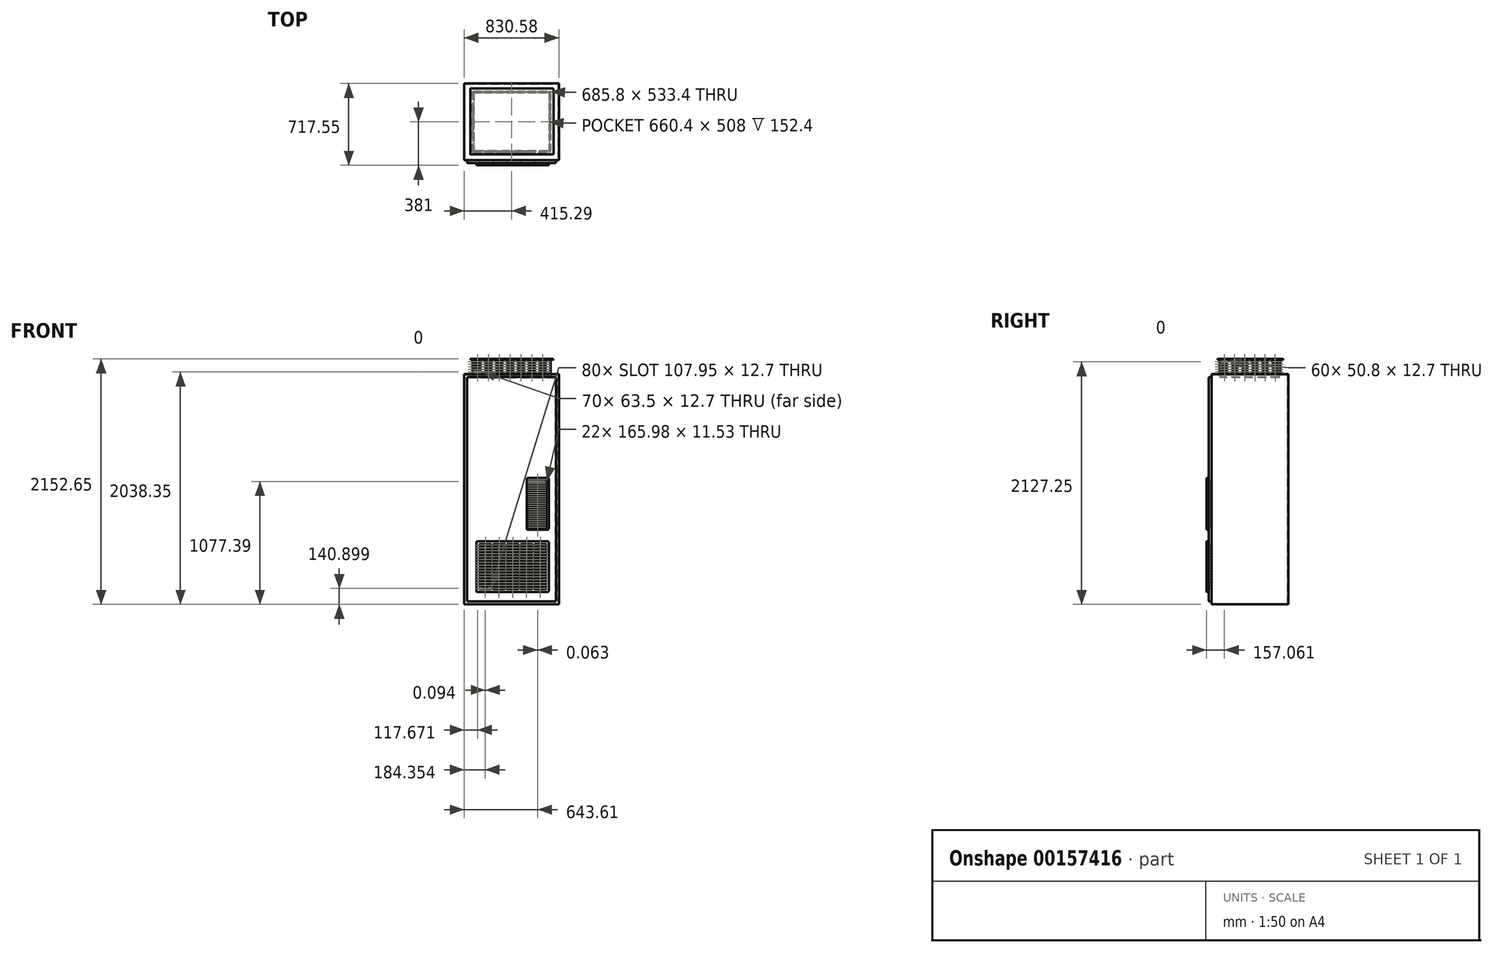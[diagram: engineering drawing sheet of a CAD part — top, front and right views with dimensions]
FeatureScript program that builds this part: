
annotation { "Feature Type Name" : "Feature", "Feature Type Description" : "" }
export const myFeature = defineFeature(function(context is Context, id is Id, definition is map)
    precondition{}
    {
        {
            var Q0;
            Q0=qCreatedBy(makeId("Front.planeOp"),FACE);
            var sketch = newSketch(context, id + "F0", { "sketchPlane" : qUnion([Q0])});
            skLineSegment(sketch, "E0.bottom", {"start": v(0, 0) * mm, "end": v(830.58, 0) * mm});
            skLineSegment(sketch, "E0.top", {"start": v(0, 2019.3) * mm, "end": v(830.58, 2019.3) * mm});
            skLineSegment(sketch, "E0.left", {"start": v(0, 0) * mm, "end": v(0, 2019.3) * mm});
            skLineSegment(sketch, "E0.right", {"start": v(830.58, 0) * mm, "end": v(830.58, 2019.3) * mm});
            skSolve(sketch);
        }
        {
            var Q0;
            Q0 = qSketchRegion(id + "F0", true);
            extrude(context, id + "F1", {"entities" : qUnion([Q0]), "depth" : 673.1 * mm});
        }
        {
            var Q0;
            Q0=makeQuery(id+"F1.opExtrude","CAP_FACE",FACE,{"disambiguationData":[OSD([sQuery(id+"F0.wireOp",EDGE,"E0.bottom"),sQuery(id+"F0.wireOp",EDGE,"E0.top"),sQuery(id+"F0.wireOp",EDGE,"E0.left"),sQuery(id+"F0.wireOp",EDGE,"E0.right")])],"isStart":false});
            var sketch = newSketch(context, id + "F2", { "sketchPlane" : qUnion([Q0])});
            skLineSegment(sketch, "E1.bottom", {"start": v(25.4, 25.4) * mm, "end": v(805.18, 25.4) * mm});
            skLineSegment(sketch, "E1.top", {"start": v(25.4, 1993.9) * mm, "end": v(805.18, 1993.9) * mm});
            skLineSegment(sketch, "E1.left", {"start": v(25.4, 25.4) * mm, "end": v(25.4, 1993.9) * mm});
            skLineSegment(sketch, "E1.right", {"start": v(805.18, 25.4) * mm, "end": v(805.18, 1993.9) * mm});
            skSolve(sketch);
        }
        {
            var Q0;
            Q0 = qSketchRegion(id + "F2", true);
            extrude(context, id + "F3", {"entities" : qUnion([Q0]), "operationType" : NewBodyOperationType.ADD, "depth" : 25.4 * mm});
        }
        {
            var Q0;
            Q0=makeQuery(id+"F3.opExtrude","CAP_EDGE",EDGE,{"disambiguationData":[OSD([sQuery(id+"F2.wireOp",EDGE,"E1.bottom")])],"isStart":false});
            var Q1;
            Q1=makeQuery(id+"F3.opExtrude","CAP_EDGE",EDGE,{"disambiguationData":[OSD([sQuery(id+"F2.wireOp",EDGE,"E1.left")])],"isStart":false});
            var Q2;
            Q2=makeQuery(id+"F3.opExtrude","CAP_EDGE",EDGE,{"disambiguationData":[OSD([sQuery(id+"F2.wireOp",EDGE,"E1.right")])],"isStart":false});
            var Q3;
            Q3=makeQuery(id+"F3.opExtrude","CAP_EDGE",EDGE,{"disambiguationData":[OSD([sQuery(id+"F2.wireOp",EDGE,"E1.top")])],"isStart":false});
            var Q4;
            Q4=makeQuery(id+"F3.opExtrude","SWEPT_EDGE",EDGE,{"disambiguationData":[OSD([sQuery(id+"F2.wireOp",EDGE,"E1.top"),sQuery(id+"F2.wireOp",EDGE,"E1.left")])]});
            var Q5;
            Q5=makeQuery(id+"F3.opExtrude","SWEPT_EDGE",EDGE,{"disambiguationData":[OSD([sQuery(id+"F2.wireOp",EDGE,"E1.top"),sQuery(id+"F2.wireOp",EDGE,"E1.right")])]});
            var Q6;
            Q6=makeQuery(id+"F3.opExtrude","SWEPT_EDGE",EDGE,{"disambiguationData":[OSD([sQuery(id+"F2.wireOp",EDGE,"E1.bottom"),sQuery(id+"F2.wireOp",EDGE,"E1.right")])]});
            var Q7;
            Q7=makeQuery(id+"F3.opExtrude","SWEPT_EDGE",EDGE,{"disambiguationData":[OSD([sQuery(id+"F2.wireOp",EDGE,"E1.bottom"),sQuery(id+"F2.wireOp",EDGE,"E1.left")])]});
            fillet(context, id + "F4", {"entities" : qUnion([Q0, Q1, Q2, Q3, Q4, Q5, Q6, Q7]), "radius" : 9.52 * mm, "tangentPropagation" : true, "allowEdgeOverflow" : false});
        }
        {
            var Q0;
            Q0=makeQuery(id+"F1.opExtrude","SWEPT_FACE",FACE,{"disambiguationData":[OSD([sQuery(id+"F0.wireOp",EDGE,"E0.top")])]});
            var sketch = newSketch(context, id + "F5", { "sketchPlane" : qUnion([Q0])});
            skLineSegment(sketch, "E2.bottom", {"start": v(72.39, -603.25) * mm, "end": v(758.19, -603.25) * mm});
            skLineSegment(sketch, "E2.top", {"start": v(72.39, -69.85) * mm, "end": v(758.19, -69.85) * mm});
            skLineSegment(sketch, "E2.left", {"start": v(72.39, -603.25) * mm, "end": v(72.39, -69.85) * mm});
            skLineSegment(sketch, "E2.right", {"start": v(758.19, -603.25) * mm, "end": v(758.19, -69.85) * mm});
            skSolve(sketch);
        }
        {
            var Q0;
            Q0 = qSketchRegion(id + "F5", true);
            extrude(context, id + "F6", {"entities" : qUnion([Q0]), "operationType" : NewBodyOperationType.ADD, "depth" : 127 * mm});
        }
        {
            var Q0;
            Q0=makeQuery(id+"F6.opExtrude","SWEPT_FACE",FACE,{"disambiguationData":[OSD([sQuery(id+"F5.wireOp",EDGE,"E2.bottom")])]});
            var sketch = newSketch(context, id + "F7", { "sketchPlane" : qUnion([Q0])});
            skLineSegment(sketch, "E3.bottom", {"start": v(85.92, 2133.6) * mm, "end": v(149.42, 2133.6) * mm});
            skLineSegment(sketch, "E3.top", {"start": v(85.92, 2120.9) * mm, "end": v(149.42, 2120.9) * mm});
            skLineSegment(sketch, "E3.left", {"start": v(85.92, 2133.6) * mm, "end": v(85.92, 2120.9) * mm});
            skLineSegment(sketch, "E3.right", {"start": v(149.42, 2133.6) * mm, "end": v(149.42, 2120.9) * mm});
            skLineSegment(sketch, "E4.bottom", {"start": v(85.92, 2111.38) * mm, "end": v(149.42, 2111.38) * mm});
            skLineSegment(sketch, "E4.top", {"start": v(85.92, 2098.67) * mm, "end": v(149.42, 2098.67) * mm});
            skLineSegment(sketch, "E4.left", {"start": v(85.92, 2111.38) * mm, "end": v(85.92, 2098.67) * mm});
            skLineSegment(sketch, "E4.right", {"start": v(149.42, 2111.38) * mm, "end": v(149.42, 2098.67) * mm});
            skLineSegment(sketch, "E5.bottom", {"start": v(85.92, 2089.15) * mm, "end": v(149.42, 2089.15) * mm});
            skLineSegment(sketch, "E5.top", {"start": v(85.92, 2076.45) * mm, "end": v(149.42, 2076.45) * mm});
            skLineSegment(sketch, "E5.left", {"start": v(85.92, 2089.15) * mm, "end": v(85.92, 2076.45) * mm});
            skLineSegment(sketch, "E5.right", {"start": v(149.42, 2089.15) * mm, "end": v(149.42, 2076.45) * mm});
            skLineSegment(sketch, "E6.bottom", {"start": v(85.92, 2066.92) * mm, "end": v(149.42, 2066.92) * mm});
            skLineSegment(sketch, "E6.top", {"start": v(85.92, 2054.22) * mm, "end": v(149.42, 2054.22) * mm});
            skLineSegment(sketch, "E6.left", {"start": v(85.92, 2066.92) * mm, "end": v(85.92, 2054.22) * mm});
            skLineSegment(sketch, "E6.right", {"start": v(149.42, 2066.92) * mm, "end": v(149.42, 2054.22) * mm});
            skLineSegment(sketch, "E7.bottom", {"start": v(85.92, 2044.7) * mm, "end": v(149.42, 2044.7) * mm});
            skLineSegment(sketch, "E7.top", {"start": v(85.92, 2032) * mm, "end": v(149.42, 2032) * mm});
            skLineSegment(sketch, "E7.left", {"start": v(85.92, 2044.7) * mm, "end": v(85.92, 2032) * mm});
            skLineSegment(sketch, "E7.right", {"start": v(149.42, 2044.7) * mm, "end": v(149.42, 2032) * mm});
            skLineSegment(sketch, "E8.1.0.0", {"start": v(181.17, 2044.7) * mm, "end": v(244.67, 2044.7) * mm});
            skLineSegment(sketch, "E8.1.0.1", {"start": v(181.17, 2066.92) * mm, "end": v(244.67, 2066.92) * mm});
            skLineSegment(sketch, "E8.1.0.2", {"start": v(181.17, 2120.9) * mm, "end": v(244.67, 2120.9) * mm});
            skLineSegment(sketch, "E8.1.0.3", {"start": v(181.17, 2133.6) * mm, "end": v(244.67, 2133.6) * mm});
            skLineSegment(sketch, "E8.1.0.4", {"start": v(181.17, 2054.22) * mm, "end": v(244.67, 2054.22) * mm});
            skLineSegment(sketch, "E8.1.0.5", {"start": v(181.17, 2111.38) * mm, "end": v(181.17, 2098.67) * mm});
            skLineSegment(sketch, "E8.1.0.6", {"start": v(181.17, 2133.6) * mm, "end": v(181.17, 2120.9) * mm});
            skLineSegment(sketch, "E8.1.0.7", {"start": v(181.17, 2044.7) * mm, "end": v(181.17, 2032) * mm});
            skLineSegment(sketch, "E8.1.0.8", {"start": v(181.17, 2089.15) * mm, "end": v(244.67, 2089.15) * mm});
            skLineSegment(sketch, "E8.1.0.9", {"start": v(244.67, 2133.6) * mm, "end": v(244.67, 2120.9) * mm});
            skLineSegment(sketch, "E8.1.0.10", {"start": v(181.17, 2111.38) * mm, "end": v(244.67, 2111.38) * mm});
            skLineSegment(sketch, "E8.1.0.11", {"start": v(244.67, 2111.38) * mm, "end": v(244.67, 2098.67) * mm});
            skLineSegment(sketch, "E8.1.0.12", {"start": v(244.67, 2044.7) * mm, "end": v(244.67, 2032) * mm});
            skLineSegment(sketch, "E8.1.0.13", {"start": v(181.17, 2032) * mm, "end": v(244.67, 2032) * mm});
            skLineSegment(sketch, "E8.1.0.14", {"start": v(181.17, 2066.92) * mm, "end": v(181.17, 2054.22) * mm});
            skLineSegment(sketch, "E8.1.0.15", {"start": v(244.67, 2066.92) * mm, "end": v(244.67, 2054.22) * mm});
            skLineSegment(sketch, "E8.1.0.16", {"start": v(244.67, 2089.15) * mm, "end": v(244.67, 2076.45) * mm});
            skLineSegment(sketch, "E8.1.0.17", {"start": v(181.17, 2098.67) * mm, "end": v(244.67, 2098.67) * mm});
            skLineSegment(sketch, "E8.1.0.18", {"start": v(181.17, 2076.45) * mm, "end": v(244.67, 2076.45) * mm});
            skLineSegment(sketch, "E8.1.0.19", {"start": v(181.17, 2089.15) * mm, "end": v(181.17, 2076.45) * mm});
            skLineSegment(sketch, "E8.2.0.0", {"start": v(276.42, 2044.7) * mm, "end": v(339.92, 2044.7) * mm});
            skLineSegment(sketch, "E8.2.0.1", {"start": v(276.42, 2066.92) * mm, "end": v(339.92, 2066.92) * mm});
            skLineSegment(sketch, "E8.2.0.2", {"start": v(276.42, 2120.9) * mm, "end": v(339.92, 2120.9) * mm});
            skLineSegment(sketch, "E8.2.0.3", {"start": v(276.42, 2133.6) * mm, "end": v(339.92, 2133.6) * mm});
            skLineSegment(sketch, "E8.2.0.4", {"start": v(276.42, 2054.22) * mm, "end": v(339.92, 2054.22) * mm});
            skLineSegment(sketch, "E8.2.0.5", {"start": v(276.42, 2111.38) * mm, "end": v(276.42, 2098.67) * mm});
            skLineSegment(sketch, "E8.2.0.6", {"start": v(276.42, 2133.6) * mm, "end": v(276.42, 2120.9) * mm});
            skLineSegment(sketch, "E8.2.0.7", {"start": v(276.42, 2044.7) * mm, "end": v(276.42, 2032) * mm});
            skLineSegment(sketch, "E8.2.0.8", {"start": v(276.42, 2089.15) * mm, "end": v(339.92, 2089.15) * mm});
            skLineSegment(sketch, "E8.2.0.9", {"start": v(339.92, 2133.6) * mm, "end": v(339.92, 2120.9) * mm});
            skLineSegment(sketch, "E8.2.0.10", {"start": v(276.42, 2111.38) * mm, "end": v(339.92, 2111.38) * mm});
            skLineSegment(sketch, "E8.2.0.11", {"start": v(339.92, 2111.38) * mm, "end": v(339.92, 2098.67) * mm});
            skLineSegment(sketch, "E8.2.0.12", {"start": v(339.92, 2044.7) * mm, "end": v(339.92, 2032) * mm});
            skLineSegment(sketch, "E8.2.0.13", {"start": v(276.42, 2032) * mm, "end": v(339.92, 2032) * mm});
            skLineSegment(sketch, "E8.2.0.14", {"start": v(276.42, 2066.92) * mm, "end": v(276.42, 2054.22) * mm});
            skLineSegment(sketch, "E8.2.0.15", {"start": v(339.92, 2066.92) * mm, "end": v(339.92, 2054.22) * mm});
            skLineSegment(sketch, "E8.2.0.16", {"start": v(339.92, 2089.15) * mm, "end": v(339.92, 2076.45) * mm});
            skLineSegment(sketch, "E8.2.0.17", {"start": v(276.42, 2098.67) * mm, "end": v(339.92, 2098.67) * mm});
            skLineSegment(sketch, "E8.2.0.18", {"start": v(276.42, 2076.45) * mm, "end": v(339.92, 2076.45) * mm});
            skLineSegment(sketch, "E8.2.0.19", {"start": v(276.42, 2089.15) * mm, "end": v(276.42, 2076.45) * mm});
            skLineSegment(sketch, "E8.3.0.0", {"start": v(371.67, 2044.7) * mm, "end": v(435.17, 2044.7) * mm});
            skLineSegment(sketch, "E8.3.0.1", {"start": v(371.67, 2066.92) * mm, "end": v(435.17, 2066.92) * mm});
            skLineSegment(sketch, "E8.3.0.2", {"start": v(371.67, 2120.9) * mm, "end": v(435.17, 2120.9) * mm});
            skLineSegment(sketch, "E8.3.0.3", {"start": v(371.67, 2133.6) * mm, "end": v(435.17, 2133.6) * mm});
            skLineSegment(sketch, "E8.3.0.4", {"start": v(371.67, 2054.22) * mm, "end": v(435.17, 2054.22) * mm});
            skLineSegment(sketch, "E8.3.0.5", {"start": v(371.67, 2111.38) * mm, "end": v(371.67, 2098.67) * mm});
            skLineSegment(sketch, "E8.3.0.6", {"start": v(371.67, 2133.6) * mm, "end": v(371.67, 2120.9) * mm});
            skLineSegment(sketch, "E8.3.0.7", {"start": v(371.67, 2044.7) * mm, "end": v(371.67, 2032) * mm});
            skLineSegment(sketch, "E8.3.0.8", {"start": v(371.67, 2089.15) * mm, "end": v(435.17, 2089.15) * mm});
            skLineSegment(sketch, "E8.3.0.9", {"start": v(435.17, 2133.6) * mm, "end": v(435.17, 2120.9) * mm});
            skLineSegment(sketch, "E8.3.0.10", {"start": v(371.67, 2111.38) * mm, "end": v(435.17, 2111.38) * mm});
            skLineSegment(sketch, "E8.3.0.11", {"start": v(435.17, 2111.38) * mm, "end": v(435.17, 2098.67) * mm});
            skLineSegment(sketch, "E8.3.0.12", {"start": v(435.17, 2044.7) * mm, "end": v(435.17, 2032) * mm});
            skLineSegment(sketch, "E8.3.0.13", {"start": v(371.67, 2032) * mm, "end": v(435.17, 2032) * mm});
            skLineSegment(sketch, "E8.3.0.14", {"start": v(371.67, 2066.92) * mm, "end": v(371.67, 2054.22) * mm});
            skLineSegment(sketch, "E8.3.0.15", {"start": v(435.17, 2066.92) * mm, "end": v(435.17, 2054.22) * mm});
            skLineSegment(sketch, "E8.3.0.16", {"start": v(435.17, 2089.15) * mm, "end": v(435.17, 2076.45) * mm});
            skLineSegment(sketch, "E8.3.0.17", {"start": v(371.67, 2098.67) * mm, "end": v(435.17, 2098.67) * mm});
            skLineSegment(sketch, "E8.3.0.18", {"start": v(371.67, 2076.45) * mm, "end": v(435.17, 2076.45) * mm});
            skLineSegment(sketch, "E8.3.0.19", {"start": v(371.67, 2089.15) * mm, "end": v(371.67, 2076.45) * mm});
            skLineSegment(sketch, "E8.4.0.0", {"start": v(466.92, 2044.7) * mm, "end": v(530.42, 2044.7) * mm});
            skLineSegment(sketch, "E8.4.0.1", {"start": v(466.92, 2066.92) * mm, "end": v(530.42, 2066.92) * mm});
            skLineSegment(sketch, "E8.4.0.2", {"start": v(466.92, 2120.9) * mm, "end": v(530.42, 2120.9) * mm});
            skLineSegment(sketch, "E8.4.0.3", {"start": v(466.92, 2133.6) * mm, "end": v(530.42, 2133.6) * mm});
            skLineSegment(sketch, "E8.4.0.4", {"start": v(466.92, 2054.22) * mm, "end": v(530.42, 2054.22) * mm});
            skLineSegment(sketch, "E8.4.0.5", {"start": v(466.92, 2111.38) * mm, "end": v(466.92, 2098.67) * mm});
            skLineSegment(sketch, "E8.4.0.6", {"start": v(466.92, 2133.6) * mm, "end": v(466.92, 2120.9) * mm});
            skLineSegment(sketch, "E8.4.0.7", {"start": v(466.92, 2044.7) * mm, "end": v(466.92, 2032) * mm});
            skLineSegment(sketch, "E8.4.0.8", {"start": v(466.92, 2089.15) * mm, "end": v(530.42, 2089.15) * mm});
            skLineSegment(sketch, "E8.4.0.9", {"start": v(530.42, 2133.6) * mm, "end": v(530.42, 2120.9) * mm});
            skLineSegment(sketch, "E8.4.0.10", {"start": v(466.92, 2111.38) * mm, "end": v(530.42, 2111.38) * mm});
            skLineSegment(sketch, "E8.4.0.11", {"start": v(530.42, 2111.38) * mm, "end": v(530.42, 2098.67) * mm});
            skLineSegment(sketch, "E8.4.0.12", {"start": v(530.42, 2044.7) * mm, "end": v(530.42, 2032) * mm});
            skLineSegment(sketch, "E8.4.0.13", {"start": v(466.92, 2032) * mm, "end": v(530.42, 2032) * mm});
            skLineSegment(sketch, "E8.4.0.14", {"start": v(466.92, 2066.92) * mm, "end": v(466.92, 2054.22) * mm});
            skLineSegment(sketch, "E8.4.0.15", {"start": v(530.42, 2066.92) * mm, "end": v(530.42, 2054.22) * mm});
            skLineSegment(sketch, "E8.4.0.16", {"start": v(530.42, 2089.15) * mm, "end": v(530.42, 2076.45) * mm});
            skLineSegment(sketch, "E8.4.0.17", {"start": v(466.92, 2098.67) * mm, "end": v(530.42, 2098.67) * mm});
            skLineSegment(sketch, "E8.4.0.18", {"start": v(466.92, 2076.45) * mm, "end": v(530.42, 2076.45) * mm});
            skLineSegment(sketch, "E8.4.0.19", {"start": v(466.92, 2089.15) * mm, "end": v(466.92, 2076.45) * mm});
            skLineSegment(sketch, "E8.5.0.0", {"start": v(562.17, 2044.7) * mm, "end": v(625.67, 2044.7) * mm});
            skLineSegment(sketch, "E8.5.0.1", {"start": v(562.17, 2066.92) * mm, "end": v(625.67, 2066.92) * mm});
            skLineSegment(sketch, "E8.5.0.2", {"start": v(562.17, 2120.9) * mm, "end": v(625.67, 2120.9) * mm});
            skLineSegment(sketch, "E8.5.0.3", {"start": v(562.17, 2133.6) * mm, "end": v(625.67, 2133.6) * mm});
            skLineSegment(sketch, "E8.5.0.4", {"start": v(562.17, 2054.22) * mm, "end": v(625.67, 2054.22) * mm});
            skLineSegment(sketch, "E8.5.0.5", {"start": v(562.17, 2111.38) * mm, "end": v(562.17, 2098.67) * mm});
            skLineSegment(sketch, "E8.5.0.6", {"start": v(562.17, 2133.6) * mm, "end": v(562.17, 2120.9) * mm});
            skLineSegment(sketch, "E8.5.0.7", {"start": v(562.17, 2044.7) * mm, "end": v(562.17, 2032) * mm});
            skLineSegment(sketch, "E8.5.0.8", {"start": v(562.17, 2089.15) * mm, "end": v(625.67, 2089.15) * mm});
            skLineSegment(sketch, "E8.5.0.9", {"start": v(625.67, 2133.6) * mm, "end": v(625.67, 2120.9) * mm});
            skLineSegment(sketch, "E8.5.0.10", {"start": v(562.17, 2111.38) * mm, "end": v(625.67, 2111.38) * mm});
            skLineSegment(sketch, "E8.5.0.11", {"start": v(625.67, 2111.38) * mm, "end": v(625.67, 2098.67) * mm});
            skLineSegment(sketch, "E8.5.0.12", {"start": v(625.67, 2044.7) * mm, "end": v(625.67, 2032) * mm});
            skLineSegment(sketch, "E8.5.0.13", {"start": v(562.17, 2032) * mm, "end": v(625.67, 2032) * mm});
            skLineSegment(sketch, "E8.5.0.14", {"start": v(562.17, 2066.92) * mm, "end": v(562.17, 2054.22) * mm});
            skLineSegment(sketch, "E8.5.0.15", {"start": v(625.67, 2066.92) * mm, "end": v(625.67, 2054.22) * mm});
            skLineSegment(sketch, "E8.5.0.16", {"start": v(625.67, 2089.15) * mm, "end": v(625.67, 2076.45) * mm});
            skLineSegment(sketch, "E8.5.0.17", {"start": v(562.17, 2098.67) * mm, "end": v(625.67, 2098.67) * mm});
            skLineSegment(sketch, "E8.5.0.18", {"start": v(562.17, 2076.45) * mm, "end": v(625.67, 2076.45) * mm});
            skLineSegment(sketch, "E8.5.0.19", {"start": v(562.17, 2089.15) * mm, "end": v(562.17, 2076.45) * mm});
            skLineSegment(sketch, "E8.6.0.0", {"start": v(657.42, 2044.7) * mm, "end": v(720.92, 2044.7) * mm});
            skLineSegment(sketch, "E8.6.0.1", {"start": v(657.42, 2066.92) * mm, "end": v(720.92, 2066.92) * mm});
            skLineSegment(sketch, "E8.6.0.2", {"start": v(657.42, 2120.9) * mm, "end": v(720.92, 2120.9) * mm});
            skLineSegment(sketch, "E8.6.0.3", {"start": v(657.42, 2133.6) * mm, "end": v(720.92, 2133.6) * mm});
            skLineSegment(sketch, "E8.6.0.4", {"start": v(657.42, 2054.22) * mm, "end": v(720.92, 2054.22) * mm});
            skLineSegment(sketch, "E8.6.0.5", {"start": v(657.42, 2111.38) * mm, "end": v(657.42, 2098.67) * mm});
            skLineSegment(sketch, "E8.6.0.6", {"start": v(657.42, 2133.6) * mm, "end": v(657.42, 2120.9) * mm});
            skLineSegment(sketch, "E8.6.0.7", {"start": v(657.42, 2044.7) * mm, "end": v(657.42, 2032) * mm});
            skLineSegment(sketch, "E8.6.0.8", {"start": v(657.42, 2089.15) * mm, "end": v(720.92, 2089.15) * mm});
            skLineSegment(sketch, "E8.6.0.9", {"start": v(720.92, 2133.6) * mm, "end": v(720.92, 2120.9) * mm});
            skLineSegment(sketch, "E8.6.0.10", {"start": v(657.42, 2111.38) * mm, "end": v(720.92, 2111.38) * mm});
            skLineSegment(sketch, "E8.6.0.11", {"start": v(720.92, 2111.38) * mm, "end": v(720.92, 2098.67) * mm});
            skLineSegment(sketch, "E8.6.0.12", {"start": v(720.92, 2044.7) * mm, "end": v(720.92, 2032) * mm});
            skLineSegment(sketch, "E8.6.0.13", {"start": v(657.42, 2032) * mm, "end": v(720.92, 2032) * mm});
            skLineSegment(sketch, "E8.6.0.14", {"start": v(657.42, 2066.92) * mm, "end": v(657.42, 2054.22) * mm});
            skLineSegment(sketch, "E8.6.0.15", {"start": v(720.92, 2066.92) * mm, "end": v(720.92, 2054.22) * mm});
            skLineSegment(sketch, "E8.6.0.16", {"start": v(720.92, 2089.15) * mm, "end": v(720.92, 2076.45) * mm});
            skLineSegment(sketch, "E8.6.0.17", {"start": v(657.42, 2098.67) * mm, "end": v(720.92, 2098.67) * mm});
            skLineSegment(sketch, "E8.6.0.18", {"start": v(657.42, 2076.45) * mm, "end": v(720.92, 2076.45) * mm});
            skLineSegment(sketch, "E8.6.0.19", {"start": v(657.42, 2089.15) * mm, "end": v(657.42, 2076.45) * mm});
            skSolve(sketch);
        }
        {
            var Q0;
            Q0 = qSketchRegion(id + "F7", true);
            extrude(context, id + "F8", {"entities" : qUnion([Q0]), "operationType" : NewBodyOperationType.REMOVE, "endBound" : BoundingType.THROUGH_ALL, "oppositeDirection" : true, "depth" : 25.4 * mm});
        }
        {
            var Q0;
            Q0=makeQuery(id+"F6.opExtrude","SWEPT_FACE",FACE,{"disambiguationData":[OSD([sQuery(id+"F5.wireOp",EDGE,"E2.left")])]});
            var sketch = newSketch(context, id + "F9", { "sketchPlane" : qUnion([Q0])});
            skLineSegment(sketch, "E9.bottom", {"start": v(90.59, 2133.6) * mm, "end": v(141.39, 2133.6) * mm});
            skLineSegment(sketch, "E9.top", {"start": v(90.59, 2120.9) * mm, "end": v(141.39, 2120.9) * mm});
            skLineSegment(sketch, "E9.left", {"start": v(90.59, 2133.6) * mm, "end": v(90.59, 2120.9) * mm});
            skLineSegment(sketch, "E9.right", {"start": v(141.39, 2133.6) * mm, "end": v(141.39, 2120.9) * mm});
            skLineSegment(sketch, "E10.1.0.0", {"start": v(179.49, 2133.6) * mm, "end": v(230.29, 2133.6) * mm});
            skLineSegment(sketch, "E10.1.0.1", {"start": v(179.49, 2120.9) * mm, "end": v(230.29, 2120.9) * mm});
            skLineSegment(sketch, "E10.1.0.2", {"start": v(179.49, 2133.6) * mm, "end": v(179.49, 2120.9) * mm});
            skLineSegment(sketch, "E10.1.0.3", {"start": v(230.29, 2133.6) * mm, "end": v(230.29, 2120.9) * mm});
            skLineSegment(sketch, "E10.2.0.0", {"start": v(268.39, 2133.6) * mm, "end": v(319.19, 2133.6) * mm});
            skLineSegment(sketch, "E10.2.0.1", {"start": v(268.39, 2120.9) * mm, "end": v(319.19, 2120.9) * mm});
            skLineSegment(sketch, "E10.2.0.2", {"start": v(268.39, 2133.6) * mm, "end": v(268.39, 2120.9) * mm});
            skLineSegment(sketch, "E10.2.0.3", {"start": v(319.19, 2133.6) * mm, "end": v(319.19, 2120.9) * mm});
            skLineSegment(sketch, "E10.3.0.0", {"start": v(357.29, 2133.6) * mm, "end": v(408.09, 2133.6) * mm});
            skLineSegment(sketch, "E10.3.0.1", {"start": v(357.29, 2120.9) * mm, "end": v(408.09, 2120.9) * mm});
            skLineSegment(sketch, "E10.3.0.2", {"start": v(357.29, 2133.6) * mm, "end": v(357.29, 2120.9) * mm});
            skLineSegment(sketch, "E10.3.0.3", {"start": v(408.09, 2133.6) * mm, "end": v(408.09, 2120.9) * mm});
            skLineSegment(sketch, "E10.4.0.0", {"start": v(446.19, 2133.6) * mm, "end": v(496.99, 2133.6) * mm});
            skLineSegment(sketch, "E10.4.0.1", {"start": v(446.19, 2120.9) * mm, "end": v(496.99, 2120.9) * mm});
            skLineSegment(sketch, "E10.4.0.2", {"start": v(446.19, 2133.6) * mm, "end": v(446.19, 2120.9) * mm});
            skLineSegment(sketch, "E10.4.0.3", {"start": v(496.99, 2133.6) * mm, "end": v(496.99, 2120.9) * mm});
            skLineSegment(sketch, "E10.5.0.0", {"start": v(535.09, 2133.6) * mm, "end": v(585.89, 2133.6) * mm});
            skLineSegment(sketch, "E10.5.0.1", {"start": v(535.09, 2120.9) * mm, "end": v(585.89, 2120.9) * mm});
            skLineSegment(sketch, "E10.5.0.2", {"start": v(535.09, 2133.6) * mm, "end": v(535.09, 2120.9) * mm});
            skLineSegment(sketch, "E10.5.0.3", {"start": v(585.89, 2133.6) * mm, "end": v(585.89, 2120.9) * mm});
            skLineSegment(sketch, "E11.1.0.0", {"start": v(318.72, 2111.38) * mm, "end": v(318.72, 2098.68) * mm});
            skLineSegment(sketch, "E11.1.0.1", {"start": v(356.82, 2111.38) * mm, "end": v(407.62, 2111.38) * mm});
            skLineSegment(sketch, "E11.1.0.2", {"start": v(267.92, 2111.38) * mm, "end": v(267.92, 2098.68) * mm});
            skLineSegment(sketch, "E11.1.0.3", {"start": v(267.92, 2098.68) * mm, "end": v(318.72, 2098.68) * mm});
            skLineSegment(sketch, "E11.1.0.4", {"start": v(267.92, 2111.38) * mm, "end": v(318.72, 2111.38) * mm});
            skLineSegment(sketch, "E11.1.0.5", {"start": v(229.82, 2111.38) * mm, "end": v(229.82, 2098.68) * mm});
            skLineSegment(sketch, "E11.1.0.6", {"start": v(179.02, 2111.38) * mm, "end": v(179.02, 2098.68) * mm});
            skLineSegment(sketch, "E11.1.0.7", {"start": v(179.02, 2098.68) * mm, "end": v(229.82, 2098.68) * mm});
            skLineSegment(sketch, "E11.1.0.8", {"start": v(179.02, 2111.38) * mm, "end": v(229.82, 2111.38) * mm});
            skLineSegment(sketch, "E11.1.0.9", {"start": v(140.92, 2111.38) * mm, "end": v(140.92, 2098.68) * mm});
            skLineSegment(sketch, "E11.1.0.10", {"start": v(90.12, 2111.38) * mm, "end": v(90.12, 2098.68) * mm});
            skLineSegment(sketch, "E11.1.0.11", {"start": v(90.12, 2111.38) * mm, "end": v(140.92, 2111.38) * mm});
            skLineSegment(sketch, "E11.1.0.12", {"start": v(407.62, 2111.38) * mm, "end": v(407.62, 2098.68) * mm});
            skLineSegment(sketch, "E11.1.0.13", {"start": v(356.82, 2111.38) * mm, "end": v(356.82, 2098.68) * mm});
            skLineSegment(sketch, "E11.1.0.14", {"start": v(356.82, 2098.68) * mm, "end": v(407.62, 2098.68) * mm});
            skLineSegment(sketch, "E11.1.0.15", {"start": v(445.72, 2098.68) * mm, "end": v(496.52, 2098.68) * mm});
            skLineSegment(sketch, "E11.1.0.16", {"start": v(496.52, 2111.38) * mm, "end": v(496.52, 2098.68) * mm});
            skLineSegment(sketch, "E11.1.0.17", {"start": v(534.62, 2098.68) * mm, "end": v(585.42, 2098.68) * mm});
            skLineSegment(sketch, "E11.1.0.18", {"start": v(585.42, 2111.38) * mm, "end": v(585.42, 2098.68) * mm});
            skLineSegment(sketch, "E11.1.0.19", {"start": v(445.72, 2111.38) * mm, "end": v(496.52, 2111.38) * mm});
            skLineSegment(sketch, "E11.1.0.20", {"start": v(445.72, 2111.38) * mm, "end": v(445.72, 2098.68) * mm});
            skLineSegment(sketch, "E11.1.0.21", {"start": v(534.62, 2111.38) * mm, "end": v(585.42, 2111.38) * mm});
            skLineSegment(sketch, "E11.1.0.22", {"start": v(90.12, 2098.68) * mm, "end": v(140.92, 2098.68) * mm});
            skLineSegment(sketch, "E11.1.0.23", {"start": v(534.62, 2111.38) * mm, "end": v(534.62, 2098.68) * mm});
            skLineSegment(sketch, "E11.2.0.0", {"start": v(318.24, 2089.16) * mm, "end": v(318.24, 2076.46) * mm});
            skLineSegment(sketch, "E11.2.0.1", {"start": v(356.34, 2089.16) * mm, "end": v(407.14, 2089.16) * mm});
            skLineSegment(sketch, "E11.2.0.2", {"start": v(267.44, 2089.16) * mm, "end": v(267.44, 2076.46) * mm});
            skLineSegment(sketch, "E11.2.0.3", {"start": v(267.44, 2076.46) * mm, "end": v(318.24, 2076.46) * mm});
            skLineSegment(sketch, "E11.2.0.4", {"start": v(267.44, 2089.16) * mm, "end": v(318.24, 2089.16) * mm});
            skLineSegment(sketch, "E11.2.0.5", {"start": v(229.34, 2089.16) * mm, "end": v(229.34, 2076.46) * mm});
            skLineSegment(sketch, "E11.2.0.6", {"start": v(178.54, 2089.16) * mm, "end": v(178.54, 2076.46) * mm});
            skLineSegment(sketch, "E11.2.0.7", {"start": v(178.54, 2076.46) * mm, "end": v(229.34, 2076.46) * mm});
            skLineSegment(sketch, "E11.2.0.8", {"start": v(178.54, 2089.16) * mm, "end": v(229.34, 2089.16) * mm});
            skLineSegment(sketch, "E11.2.0.9", {"start": v(140.44, 2089.16) * mm, "end": v(140.44, 2076.46) * mm});
            skLineSegment(sketch, "E11.2.0.10", {"start": v(89.64, 2089.16) * mm, "end": v(89.64, 2076.46) * mm});
            skLineSegment(sketch, "E11.2.0.11", {"start": v(89.64, 2089.16) * mm, "end": v(140.44, 2089.16) * mm});
            skLineSegment(sketch, "E11.2.0.12", {"start": v(407.14, 2089.16) * mm, "end": v(407.14, 2076.46) * mm});
            skLineSegment(sketch, "E11.2.0.13", {"start": v(356.34, 2089.16) * mm, "end": v(356.34, 2076.46) * mm});
            skLineSegment(sketch, "E11.2.0.14", {"start": v(356.34, 2076.46) * mm, "end": v(407.14, 2076.46) * mm});
            skLineSegment(sketch, "E11.2.0.15", {"start": v(445.24, 2076.46) * mm, "end": v(496.04, 2076.46) * mm});
            skLineSegment(sketch, "E11.2.0.16", {"start": v(496.04, 2089.16) * mm, "end": v(496.04, 2076.46) * mm});
            skLineSegment(sketch, "E11.2.0.17", {"start": v(534.14, 2076.46) * mm, "end": v(584.94, 2076.46) * mm});
            skLineSegment(sketch, "E11.2.0.18", {"start": v(584.94, 2089.16) * mm, "end": v(584.94, 2076.46) * mm});
            skLineSegment(sketch, "E11.2.0.19", {"start": v(445.24, 2089.16) * mm, "end": v(496.04, 2089.16) * mm});
            skLineSegment(sketch, "E11.2.0.20", {"start": v(445.24, 2089.16) * mm, "end": v(445.24, 2076.46) * mm});
            skLineSegment(sketch, "E11.2.0.21", {"start": v(534.14, 2089.16) * mm, "end": v(584.94, 2089.16) * mm});
            skLineSegment(sketch, "E11.2.0.22", {"start": v(89.64, 2076.46) * mm, "end": v(140.44, 2076.46) * mm});
            skLineSegment(sketch, "E11.2.0.23", {"start": v(534.14, 2089.16) * mm, "end": v(534.14, 2076.46) * mm});
            skLineSegment(sketch, "E11.3.0.0", {"start": v(317.77, 2066.94) * mm, "end": v(317.77, 2054.24) * mm});
            skLineSegment(sketch, "E11.3.0.1", {"start": v(355.87, 2066.94) * mm, "end": v(406.67, 2066.94) * mm});
            skLineSegment(sketch, "E11.3.0.2", {"start": v(266.97, 2066.94) * mm, "end": v(266.97, 2054.24) * mm});
            skLineSegment(sketch, "E11.3.0.3", {"start": v(266.97, 2054.24) * mm, "end": v(317.77, 2054.24) * mm});
            skLineSegment(sketch, "E11.3.0.4", {"start": v(266.97, 2066.94) * mm, "end": v(317.77, 2066.94) * mm});
            skLineSegment(sketch, "E11.3.0.5", {"start": v(228.87, 2066.94) * mm, "end": v(228.87, 2054.24) * mm});
            skLineSegment(sketch, "E11.3.0.6", {"start": v(178.07, 2066.94) * mm, "end": v(178.07, 2054.24) * mm});
            skLineSegment(sketch, "E11.3.0.7", {"start": v(178.07, 2054.24) * mm, "end": v(228.87, 2054.24) * mm});
            skLineSegment(sketch, "E11.3.0.8", {"start": v(178.07, 2066.94) * mm, "end": v(228.87, 2066.94) * mm});
            skLineSegment(sketch, "E11.3.0.9", {"start": v(139.97, 2066.94) * mm, "end": v(139.97, 2054.24) * mm});
            skLineSegment(sketch, "E11.3.0.10", {"start": v(89.17, 2066.94) * mm, "end": v(89.17, 2054.24) * mm});
            skLineSegment(sketch, "E11.3.0.11", {"start": v(89.17, 2066.94) * mm, "end": v(139.97, 2066.94) * mm});
            skLineSegment(sketch, "E11.3.0.12", {"start": v(406.67, 2066.94) * mm, "end": v(406.67, 2054.24) * mm});
            skLineSegment(sketch, "E11.3.0.13", {"start": v(355.87, 2066.94) * mm, "end": v(355.87, 2054.24) * mm});
            skLineSegment(sketch, "E11.3.0.14", {"start": v(355.87, 2054.24) * mm, "end": v(406.67, 2054.24) * mm});
            skLineSegment(sketch, "E11.3.0.15", {"start": v(444.77, 2054.24) * mm, "end": v(495.57, 2054.24) * mm});
            skLineSegment(sketch, "E11.3.0.16", {"start": v(495.57, 2066.94) * mm, "end": v(495.57, 2054.24) * mm});
            skLineSegment(sketch, "E11.3.0.17", {"start": v(533.67, 2054.24) * mm, "end": v(584.47, 2054.24) * mm});
            skLineSegment(sketch, "E11.3.0.18", {"start": v(584.47, 2066.94) * mm, "end": v(584.47, 2054.24) * mm});
            skLineSegment(sketch, "E11.3.0.19", {"start": v(444.77, 2066.94) * mm, "end": v(495.57, 2066.94) * mm});
            skLineSegment(sketch, "E11.3.0.20", {"start": v(444.77, 2066.94) * mm, "end": v(444.77, 2054.24) * mm});
            skLineSegment(sketch, "E11.3.0.21", {"start": v(533.67, 2066.94) * mm, "end": v(584.47, 2066.94) * mm});
            skLineSegment(sketch, "E11.3.0.22", {"start": v(89.17, 2054.24) * mm, "end": v(139.97, 2054.24) * mm});
            skLineSegment(sketch, "E11.3.0.23", {"start": v(533.67, 2066.94) * mm, "end": v(533.67, 2054.24) * mm});
            skLineSegment(sketch, "E11.4.0.0", {"start": v(317.3, 2044.72) * mm, "end": v(317.3, 2032.02) * mm});
            skLineSegment(sketch, "E11.4.0.1", {"start": v(355.4, 2044.72) * mm, "end": v(406.2, 2044.72) * mm});
            skLineSegment(sketch, "E11.4.0.2", {"start": v(266.5, 2044.72) * mm, "end": v(266.5, 2032.02) * mm});
            skLineSegment(sketch, "E11.4.0.3", {"start": v(266.5, 2032.02) * mm, "end": v(317.3, 2032.02) * mm});
            skLineSegment(sketch, "E11.4.0.4", {"start": v(266.5, 2044.72) * mm, "end": v(317.3, 2044.72) * mm});
            skLineSegment(sketch, "E11.4.0.5", {"start": v(228.4, 2044.72) * mm, "end": v(228.4, 2032.02) * mm});
            skLineSegment(sketch, "E11.4.0.6", {"start": v(177.6, 2044.72) * mm, "end": v(177.6, 2032.02) * mm});
            skLineSegment(sketch, "E11.4.0.7", {"start": v(177.6, 2032.02) * mm, "end": v(228.4, 2032.02) * mm});
            skLineSegment(sketch, "E11.4.0.8", {"start": v(177.6, 2044.72) * mm, "end": v(228.4, 2044.72) * mm});
            skLineSegment(sketch, "E11.4.0.9", {"start": v(139.5, 2044.72) * mm, "end": v(139.5, 2032.02) * mm});
            skLineSegment(sketch, "E11.4.0.10", {"start": v(88.7, 2044.72) * mm, "end": v(88.7, 2032.02) * mm});
            skLineSegment(sketch, "E11.4.0.11", {"start": v(88.7, 2044.72) * mm, "end": v(139.5, 2044.72) * mm});
            skLineSegment(sketch, "E11.4.0.12", {"start": v(406.2, 2044.72) * mm, "end": v(406.2, 2032.02) * mm});
            skLineSegment(sketch, "E11.4.0.13", {"start": v(355.4, 2044.72) * mm, "end": v(355.4, 2032.02) * mm});
            skLineSegment(sketch, "E11.4.0.14", {"start": v(355.4, 2032.02) * mm, "end": v(406.2, 2032.02) * mm});
            skLineSegment(sketch, "E11.4.0.15", {"start": v(444.3, 2032.02) * mm, "end": v(495.1, 2032.02) * mm});
            skLineSegment(sketch, "E11.4.0.16", {"start": v(495.1, 2044.72) * mm, "end": v(495.1, 2032.02) * mm});
            skLineSegment(sketch, "E11.4.0.17", {"start": v(533.2, 2032.02) * mm, "end": v(584, 2032.02) * mm});
            skLineSegment(sketch, "E11.4.0.18", {"start": v(584, 2044.72) * mm, "end": v(584, 2032.02) * mm});
            skLineSegment(sketch, "E11.4.0.19", {"start": v(444.3, 2044.72) * mm, "end": v(495.1, 2044.72) * mm});
            skLineSegment(sketch, "E11.4.0.20", {"start": v(444.3, 2044.72) * mm, "end": v(444.3, 2032.02) * mm});
            skLineSegment(sketch, "E11.4.0.21", {"start": v(533.2, 2044.72) * mm, "end": v(584, 2044.72) * mm});
            skLineSegment(sketch, "E11.4.0.22", {"start": v(88.7, 2032.02) * mm, "end": v(139.5, 2032.02) * mm});
            skLineSegment(sketch, "E11.4.0.23", {"start": v(533.2, 2044.72) * mm, "end": v(533.2, 2032.02) * mm});
            skLineSegment(sketch, "E11.direction1", {"start": v(90.59, 2120.9) * mm, "end": v(90.12, 2098.68) * mm, "construction": true});
            skSolve(sketch);
        }
        {
            var Q0;
            Q0=makeQuery(id+"F9.imprint","IMPRINT",FACE,{"disambiguationData":[TD([[makeQuery(id+"F9.imprint","IMPRINT",EDGE,{"derivedFrom":sQuery(id+"F9.wireOp",EDGE,"E11.3.0.9")}),-1.0]])]});
            var Q1;
            Q1=makeQuery(id+"F9.imprint","IMPRINT",FACE,{"disambiguationData":[TD([[makeQuery(id+"F9.imprint","IMPRINT",EDGE,{"derivedFrom":sQuery(id+"F9.wireOp",EDGE,"E11.3.0.15")}),1.0]])]});
            var Q2;
            Q2=makeQuery(id+"F9.imprint","IMPRINT",FACE,{"disambiguationData":[TD([[makeQuery(id+"F9.imprint","IMPRINT",EDGE,{"derivedFrom":sQuery(id+"F9.wireOp",EDGE,"E11.4.0.15")}),1.0]])]});
            var Q3;
            Q3=makeQuery(id+"F9.imprint","IMPRINT",FACE,{"disambiguationData":[TD([[makeQuery(id+"F9.imprint","IMPRINT",EDGE,{"derivedFrom":sQuery(id+"F9.wireOp",EDGE,"E11.3.0.5")}),-1.0]])]});
            var Q4;
            Q4=makeQuery(id+"F9.imprint","IMPRINT",FACE,{"disambiguationData":[TD([[makeQuery(id+"F9.imprint","IMPRINT",EDGE,{"derivedFrom":sQuery(id+"F9.wireOp",EDGE,"E11.4.0.17")}),1.0]])]});
            var Q5;
            Q5=makeQuery(id+"F9.imprint","IMPRINT",FACE,{"disambiguationData":[TD([[makeQuery(id+"F9.imprint","IMPRINT",EDGE,{"derivedFrom":sQuery(id+"F9.wireOp",EDGE,"E11.2.0.0")}),-1.0]])]});
            var Q6;
            Q6=makeQuery(id+"F9.imprint","IMPRINT",FACE,{"disambiguationData":[TD([[makeQuery(id+"F9.imprint","IMPRINT",EDGE,{"derivedFrom":sQuery(id+"F9.wireOp",EDGE,"E11.1.0.17")}),1.0]])]});
            var Q7;
            Q7=makeQuery(id+"F9.imprint","IMPRINT",FACE,{"disambiguationData":[TD([[makeQuery(id+"F9.imprint","IMPRINT",EDGE,{"derivedFrom":sQuery(id+"F9.wireOp",EDGE,"E11.1.0.15")}),1.0]])]});
            var Q8;
            Q8=makeQuery(id+"F9.imprint","IMPRINT",FACE,{"disambiguationData":[TD([[makeQuery(id+"F9.imprint","IMPRINT",EDGE,{"derivedFrom":sQuery(id+"F9.wireOp",EDGE,"E11.1.0.9")}),-1.0]])]});
            var Q9;
            Q9=makeQuery(id+"F9.imprint","IMPRINT",FACE,{"disambiguationData":[TD([[makeQuery(id+"F9.imprint","IMPRINT",EDGE,{"derivedFrom":sQuery(id+"F9.wireOp",EDGE,"E11.1.0.5")}),-1.0]])]});
            var Q10;
            Q10=makeQuery(id+"F9.imprint","IMPRINT",FACE,{"disambiguationData":[TD([[makeQuery(id+"F9.imprint","IMPRINT",EDGE,{"derivedFrom":sQuery(id+"F9.wireOp",EDGE,"E11.1.0.1")}),-1.0]])]});
            var Q11;
            Q11=makeQuery(id+"F9.imprint","IMPRINT",FACE,{"disambiguationData":[TD([[makeQuery(id+"F9.imprint","IMPRINT",EDGE,{"derivedFrom":sQuery(id+"F9.wireOp",EDGE,"E11.1.0.0")}),-1.0]])]});
            var Q12;
            Q12=makeQuery(id+"F9.imprint","IMPRINT",FACE,{"disambiguationData":[TD([[makeQuery(id+"F9.imprint","IMPRINT",EDGE,{"derivedFrom":sQuery(id+"F9.wireOp",EDGE,"E11.4.0.9")}),-1.0]])]});
            var Q13;
            Q13=makeQuery(id+"F9.imprint","IMPRINT",FACE,{"disambiguationData":[TD([[makeQuery(id+"F9.imprint","IMPRINT",EDGE,{"derivedFrom":sQuery(id+"F9.wireOp",EDGE,"E10.5.0.0")}),-1.0]])]});
            var Q14;
            Q14=makeQuery(id+"F9.imprint","IMPRINT",FACE,{"disambiguationData":[TD([[makeQuery(id+"F9.imprint","IMPRINT",EDGE,{"derivedFrom":sQuery(id+"F9.wireOp",EDGE,"E10.4.0.0")}),-1.0]])]});
            var Q15;
            Q15=makeQuery(id+"F9.imprint","IMPRINT",FACE,{"disambiguationData":[TD([[makeQuery(id+"F9.imprint","IMPRINT",EDGE,{"derivedFrom":sQuery(id+"F9.wireOp",EDGE,"E10.3.0.0")}),-1.0]])]});
            var Q16;
            Q16=makeQuery(id+"F9.imprint","IMPRINT",FACE,{"disambiguationData":[TD([[makeQuery(id+"F9.imprint","IMPRINT",EDGE,{"derivedFrom":sQuery(id+"F9.wireOp",EDGE,"E10.2.0.0")}),-1.0]])]});
            var Q17;
            Q17=makeQuery(id+"F9.imprint","IMPRINT",FACE,{"disambiguationData":[TD([[makeQuery(id+"F9.imprint","IMPRINT",EDGE,{"derivedFrom":sQuery(id+"F9.wireOp",EDGE,"E10.1.0.0")}),-1.0]])]});
            var Q18;
            Q18=makeQuery(id+"F9.imprint","IMPRINT",FACE,{"disambiguationData":[TD([[makeQuery(id+"F9.imprint","IMPRINT",EDGE,{"derivedFrom":sQuery(id+"F9.wireOp",EDGE,"E9.bottom")}),-1.0]])]});
            var Q19;
            Q19=makeQuery(id+"F9.imprint","IMPRINT",FACE,{"disambiguationData":[TD([[makeQuery(id+"F9.imprint","IMPRINT",EDGE,{"derivedFrom":sQuery(id+"F9.wireOp",EDGE,"E11.2.0.5")}),-1.0]])]});
            var Q20;
            Q20=makeQuery(id+"F9.imprint","IMPRINT",FACE,{"disambiguationData":[TD([[makeQuery(id+"F9.imprint","IMPRINT",EDGE,{"derivedFrom":sQuery(id+"F9.wireOp",EDGE,"E11.2.0.1")}),-1.0]])]});
            var Q21;
            Q21=makeQuery(id+"F9.imprint","IMPRINT",FACE,{"disambiguationData":[TD([[makeQuery(id+"F9.imprint","IMPRINT",EDGE,{"derivedFrom":sQuery(id+"F9.wireOp",EDGE,"E11.2.0.9")}),-1.0]])]});
            var Q22;
            Q22=makeQuery(id+"F9.imprint","IMPRINT",FACE,{"disambiguationData":[TD([[makeQuery(id+"F9.imprint","IMPRINT",EDGE,{"derivedFrom":sQuery(id+"F9.wireOp",EDGE,"E11.3.0.1")}),-1.0]])]});
            var Q23;
            Q23=makeQuery(id+"F9.imprint","IMPRINT",FACE,{"disambiguationData":[TD([[makeQuery(id+"F9.imprint","IMPRINT",EDGE,{"derivedFrom":sQuery(id+"F9.wireOp",EDGE,"E11.4.0.5")}),-1.0]])]});
            var Q24;
            Q24=makeQuery(id+"F9.imprint","IMPRINT",FACE,{"disambiguationData":[TD([[makeQuery(id+"F9.imprint","IMPRINT",EDGE,{"derivedFrom":sQuery(id+"F9.wireOp",EDGE,"E11.3.0.0")}),-1.0]])]});
            var Q25;
            Q25=makeQuery(id+"F9.imprint","IMPRINT",FACE,{"disambiguationData":[TD([[makeQuery(id+"F9.imprint","IMPRINT",EDGE,{"derivedFrom":sQuery(id+"F9.wireOp",EDGE,"E11.4.0.1")}),-1.0]])]});
            var Q26;
            Q26=makeQuery(id+"F9.imprint","IMPRINT",FACE,{"disambiguationData":[TD([[makeQuery(id+"F9.imprint","IMPRINT",EDGE,{"derivedFrom":sQuery(id+"F9.wireOp",EDGE,"E11.2.0.17")}),1.0]])]});
            var Q27;
            Q27=makeQuery(id+"F9.imprint","IMPRINT",FACE,{"disambiguationData":[TD([[makeQuery(id+"F9.imprint","IMPRINT",EDGE,{"derivedFrom":sQuery(id+"F9.wireOp",EDGE,"E11.4.0.0")}),-1.0]])]});
            var Q28;
            Q28=makeQuery(id+"F9.imprint","IMPRINT",FACE,{"disambiguationData":[TD([[makeQuery(id+"F9.imprint","IMPRINT",EDGE,{"derivedFrom":sQuery(id+"F9.wireOp",EDGE,"E11.2.0.15")}),1.0]])]});
            var Q29;
            Q29=makeQuery(id+"F9.imprint","IMPRINT",FACE,{"disambiguationData":[TD([[makeQuery(id+"F9.imprint","IMPRINT",EDGE,{"derivedFrom":sQuery(id+"F9.wireOp",EDGE,"E11.3.0.17")}),1.0]])]});
            var Q30;
            Q30=sQuery(id+"F9.wireOp",EDGE,"E11.4.0.22");
            var Q31;
            Q31=sQuery(id+"F9.wireOp",EDGE,"E11.4.0.15");
            var Q32;
            Q32=sQuery(id+"F9.wireOp",EDGE,"E11.2.0.6");
            var Q33;
            Q33=sQuery(id+"F9.wireOp",EDGE,"E11.1.0.23");
            var Q34;
            Q34=sQuery(id+"F9.wireOp",EDGE,"E11.2.0.22");
            var Q35;
            Q35=sQuery(id+"F9.wireOp",EDGE,"E11.2.0.15");
            var Q36;
            Q36=sQuery(id+"F9.wireOp",EDGE,"E11.3.0.14");
            var Q37;
            Q37=sQuery(id+"F9.wireOp",EDGE,"E11.3.0.7");
            var Q38;
            Q38=sQuery(id+"F9.wireOp",EDGE,"E10.5.0.2");
            var Q39;
            Q39=sQuery(id+"F9.wireOp",EDGE,"E11.4.0.6");
            var Q40;
            Q40=sQuery(id+"F9.wireOp",EDGE,"E11.3.0.23");
            var Q41;
            Q41=sQuery(id+"F9.wireOp",EDGE,"E11.3.0.20");
            var Q42;
            Q42=sQuery(id+"F9.wireOp",EDGE,"E11.4.0.12");
            var Q43;
            Q43=sQuery(id+"F9.wireOp",EDGE,"E11.1.0.20");
            var Q44;
            Q44=sQuery(id+"F9.wireOp",EDGE,"E11.1.0.4");
            var Q45;
            Q45=sQuery(id+"F9.wireOp",EDGE,"E11.2.0.12");
            var Q46;
            Q46=sQuery(id+"F9.wireOp",EDGE,"E11.3.0.4");
            var Q47;
            Q47=sQuery(id+"F9.wireOp",EDGE,"E11.1.0.7");
            var Q48;
            Q48=sQuery(id+"F9.wireOp",EDGE,"E11.1.0.14");
            var Q49;
            Q49=sQuery(id+"F9.wireOp",EDGE,"E11.4.0.21");
            var Q50;
            Q50=sQuery(id+"F9.wireOp",EDGE,"E11.4.0.14");
            var Q51;
            Q51=sQuery(id+"F9.wireOp",EDGE,"E11.2.0.5");
            var Q52;
            Q52=sQuery(id+"F9.wireOp",EDGE,"E11.1.0.22");
            var Q53;
            Q53=sQuery(id+"F9.wireOp",EDGE,"E11.2.0.21");
            var Q54;
            Q54=sQuery(id+"F9.wireOp",EDGE,"E11.2.0.14");
            var Q55;
            Q55=sQuery(id+"F9.wireOp",EDGE,"E11.3.0.6");
            var Q56;
            Q56=sQuery(id+"F9.wireOp",EDGE,"E11.4.0.5");
            var Q57;
            Q57=sQuery(id+"F9.wireOp",EDGE,"E11.3.0.22");
            var Q58;
            Q58=sQuery(id+"F9.wireOp",EDGE,"E10.5.0.1");
            var Q59;
            Q59=sQuery(id+"F9.wireOp",EDGE,"E11.1.0.13");
            var Q60;
            Q60=sQuery(id+"F9.wireOp",EDGE,"E11.1.0.6");
            var Q61;
            Q61=sQuery(id+"F9.wireOp",EDGE,"E11.3.0.19");
            var Q62;
            Q62=sQuery(id+"F9.wireOp",EDGE,"E11.4.0.11");
            var Q63;
            Q63=sQuery(id+"F9.wireOp",EDGE,"E11.1.0.3");
            var Q64;
            Q64=sQuery(id+"F9.wireOp",EDGE,"E11.1.0.19");
            var Q65;
            Q65=sQuery(id+"F9.wireOp",EDGE,"E11.2.0.11");
            var Q66;
            Q66=sQuery(id+"F9.wireOp",EDGE,"E11.3.0.3");
            var Q67;
            Q67=sQuery(id+"F9.wireOp",EDGE,"E11.4.0.20");
            var Q68;
            Q68=sQuery(id+"F9.wireOp",EDGE,"E11.4.0.13");
            var Q69;
            Q69=sQuery(id+"F9.wireOp",EDGE,"E11.2.0.4");
            var Q70;
            Q70=sQuery(id+"F9.wireOp",EDGE,"E11.1.0.21");
            var Q71;
            Q71=sQuery(id+"F9.wireOp",EDGE,"E11.2.0.20");
            var Q72;
            Q72=sQuery(id+"F9.wireOp",EDGE,"E11.2.0.13");
            var Q73;
            Q73=sQuery(id+"F9.wireOp",EDGE,"E11.3.0.12");
            var Q74;
            Q74=sQuery(id+"F9.wireOp",EDGE,"E11.3.0.5");
            var Q75;
            Q75=sQuery(id+"F9.wireOp",EDGE,"E11.4.0.4");
            var Q76;
            Q76=sQuery(id+"F9.wireOp",EDGE,"E11.3.0.21");
            var Q77;
            Q77=sQuery(id+"F9.wireOp",EDGE,"E10.5.0.0");
            var Q78;
            Q78=sQuery(id+"F9.wireOp",EDGE,"E11.1.0.12");
            var Q79;
            Q79=sQuery(id+"F9.wireOp",EDGE,"E11.1.0.5");
            var Q80;
            Q80=sQuery(id+"F9.wireOp",EDGE,"E10.3.0.0");
            var Q81;
            Q81=sQuery(id+"F9.wireOp",EDGE,"E10.2.0.3");
            var Q82;
            Q82=sQuery(id+"F9.wireOp",EDGE,"E10.2.0.2");
            var Q83;
            Q83=sQuery(id+"F9.wireOp",EDGE,"E10.2.0.1");
            var Q84;
            Q84=sQuery(id+"F9.wireOp",EDGE,"E10.2.0.0");
            var Q85;
            Q85=sQuery(id+"F9.wireOp",EDGE,"E11.3.0.18");
            var Q86;
            Q86=sQuery(id+"F9.wireOp",EDGE,"E11.4.0.10");
            var Q87;
            Q87=sQuery(id+"F9.wireOp",EDGE,"E10.1.0.3");
            var Q88;
            Q88=sQuery(id+"F9.wireOp",EDGE,"E11.1.0.18");
            var Q89;
            Q89=sQuery(id+"F9.wireOp",EDGE,"E11.2.0.10");
            var Q90;
            Q90=sQuery(id+"F9.wireOp",EDGE,"E11.3.0.2");
            var Q91;
            Q91=sQuery(id+"F9.wireOp",EDGE,"E10.1.0.1");
            var Q92;
            Q92=sQuery(id+"F9.wireOp",EDGE,"E10.1.0.0");
            var Q93;
            Q93=sQuery(id+"F9.wireOp",EDGE,"E9.right");
            var Q94;
            Q94=sQuery(id+"F9.wireOp",EDGE,"E9.left");
            var Q95;
            Q95=sQuery(id+"F9.wireOp",EDGE,"E9.top");
            var Q96;
            Q96=sQuery(id+"F9.wireOp",EDGE,"E9.bottom");
            var Q97;
            Q97=sQuery(id+"F9.wireOp",EDGE,"E10.3.0.3");
            var Q98;
            Q98=sQuery(id+"F9.wireOp",EDGE,"E10.3.0.2");
            var Q99;
            Q99=sQuery(id+"F9.wireOp",EDGE,"E10.3.0.1");
            var Q100;
            Q100=sQuery(id+"F9.wireOp",EDGE,"E11.4.0.19");
            var Q101;
            Q101=sQuery(id+"F9.wireOp",EDGE,"E11.2.0.3");
            var Q102;
            Q102=sQuery(id+"F9.wireOp",EDGE,"E11.2.0.19");
            var Q103;
            Q103=sQuery(id+"F9.wireOp",EDGE,"E11.3.0.11");
            var Q104;
            Q104=sQuery(id+"F9.wireOp",EDGE,"E11.4.0.3");
            var Q105;
            Q105=sQuery(id+"F9.wireOp",EDGE,"E11.1.0.11");
            var Q106;
            Q106=sQuery(id+"F9.wireOp",EDGE,"E11.3.0.17");
            var Q107;
            Q107=sQuery(id+"F9.wireOp",EDGE,"E11.1.0.1");
            var Q108;
            Q108=sQuery(id+"F9.wireOp",EDGE,"E11.1.0.17");
            var Q109;
            Q109=sQuery(id+"F9.wireOp",EDGE,"E11.2.0.9");
            var Q110;
            Q110=sQuery(id+"F9.wireOp",EDGE,"E11.3.0.1");
            var Q111;
            Q111=sQuery(id+"F9.wireOp",EDGE,"E11.4.0.18");
            var Q112;
            Q112=sQuery(id+"F9.wireOp",EDGE,"E11.2.0.2");
            var Q113;
            Q113=sQuery(id+"F9.wireOp",EDGE,"E11.3.0.10");
            var Q114;
            Q114=sQuery(id+"F9.wireOp",EDGE,"E11.4.0.2");
            var Q115;
            Q115=sQuery(id+"F9.wireOp",EDGE,"E10.4.0.2");
            var Q116;
            Q116=sQuery(id+"F9.wireOp",EDGE,"E11.3.0.16");
            var Q117;
            Q117=sQuery(id+"F9.wireOp",EDGE,"E11.4.0.8");
            var Q118;
            Q118=sQuery(id+"F9.wireOp",EDGE,"E11.1.0.0");
            var Q119;
            Q119=sQuery(id+"F9.wireOp",EDGE,"E11.1.0.16");
            var Q120;
            Q120=sQuery(id+"F9.wireOp",EDGE,"E11.2.0.8");
            var Q121;
            Q121=sQuery(id+"F9.wireOp",EDGE,"E11.3.0.0");
            var Q122;
            Q122=sQuery(id+"F9.wireOp",EDGE,"E11.4.0.17");
            var Q123;
            Q123=sQuery(id+"F9.wireOp",EDGE,"E11.2.0.1");
            var Q124;
            Q124=sQuery(id+"F9.wireOp",EDGE,"E11.2.0.17");
            var Q125;
            Q125=sQuery(id+"F9.wireOp",EDGE,"E11.3.0.9");
            var Q126;
            Q126=sQuery(id+"F9.wireOp",EDGE,"E11.4.0.1");
            var Q127;
            Q127=sQuery(id+"F9.wireOp",EDGE,"E10.4.0.1");
            var Q128;
            Q128=sQuery(id+"F9.wireOp",EDGE,"E11.1.0.9");
            var Q129;
            Q129=sQuery(id+"F9.wireOp",EDGE,"E11.3.0.15");
            var Q130;
            Q130=sQuery(id+"F9.wireOp",EDGE,"E11.4.0.7");
            var Q131;
            Q131=sQuery(id+"F9.wireOp",EDGE,"E11.4.0.23");
            var Q132;
            Q132=sQuery(id+"F9.wireOp",EDGE,"E10.5.0.3");
            var Q133;
            Q133=sQuery(id+"F9.wireOp",EDGE,"E11.1.0.15");
            var Q134;
            Q134=sQuery(id+"F9.wireOp",EDGE,"E11.2.0.7");
            var Q135;
            Q135=sQuery(id+"F9.wireOp",EDGE,"E11.2.0.23");
            var Q136;
            Q136=sQuery(id+"F9.wireOp",EDGE,"E11.4.0.16");
            var Q137;
            Q137=sQuery(id+"F9.wireOp",EDGE,"E11.2.0.0");
            var Q138;
            Q138=sQuery(id+"F9.wireOp",EDGE,"E11.2.0.16");
            var Q139;
            Q139=sQuery(id+"F9.wireOp",EDGE,"E11.3.0.8");
            var Q140;
            Q140=sQuery(id+"F9.wireOp",EDGE,"E11.4.0.0");
            var Q141;
            Q141=sQuery(id+"F9.wireOp",EDGE,"E10.4.0.0");
            var Q142;
            Q142=sQuery(id+"F9.wireOp",EDGE,"E11.1.0.8");
            var Q143;
            Q143=sQuery(id+"F9.wireOp",EDGE,"E11.1.0.10");
            var Q144;
            Q144=sQuery(id+"F9.wireOp",EDGE,"E11.3.0.13");
            var Q145;
            Q145=sQuery(id+"F9.wireOp",EDGE,"E11.1.0.2");
            var Q146;
            Q146=sQuery(id+"F9.wireOp",EDGE,"E10.1.0.2");
            var Q147;
            Q147=sQuery(id+"F9.wireOp",EDGE,"E10.4.0.3");
            var Q148;
            Q148=sQuery(id+"F9.wireOp",EDGE,"E11.4.0.9");
            var Q149;
            Q149=sQuery(id+"F9.wireOp",EDGE,"E11.2.0.18");
            extrude(context, id + "F10", {"entities" : qUnion([Q0, Q1, Q2, Q3, Q4, Q5, Q6, Q7, Q8, Q9, Q10, Q11, Q12, Q13, Q14, Q15, Q16, Q17, Q18, Q19, Q20, Q21, Q22, Q23, Q24, Q25, Q26, Q27, Q28, Q29]), "operationType" : NewBodyOperationType.REMOVE, "surfaceEntities" : qUnion([Q30, Q31, Q32, Q33, Q34, Q35, Q36, Q37, Q38, Q39, Q40, Q41, Q42, Q43, Q44, Q45, Q46, Q47, Q48, Q49, Q50, Q51, Q52, Q53, Q54, Q55, Q56, Q57, Q58, Q59, Q60, Q61, Q62, Q63, Q64, Q65, Q66, Q67, Q68, Q69, Q70, Q71, Q72, Q73, Q74, Q75, Q76, Q77, Q78, Q79, Q80, Q81, Q82, Q83, Q84, Q85, Q86, Q87, Q88, Q89, Q90, Q91, Q92, Q93, Q94, Q95, Q96, Q97, Q98, Q99, Q100, Q101, Q102, Q103, Q104, Q105, Q106, Q107, Q108, Q109, Q110, Q111, Q112, Q113, Q114, Q115, Q116, Q117, Q118, Q119, Q120, Q121, Q122, Q123, Q124, Q125, Q126, Q127, Q128, Q129, Q130, Q131, Q132, Q133, Q134, Q135, Q136, Q137, Q138, Q139, Q140, Q141, Q142, Q143, Q144, Q145, Q146, Q147, Q148, Q149]), "endBound" : BoundingType.THROUGH_ALL, "oppositeDirection" : true, "depth" : 25.4 * mm});
        }
        {
            var Q0;
            Q0=makeQuery(id+"F6.opExtrude","CAP_FACE",FACE,{"disambiguationData":[OSD([sQuery(id+"F5.wireOp",EDGE,"E2.bottom"),sQuery(id+"F5.wireOp",EDGE,"E2.top"),sQuery(id+"F5.wireOp",EDGE,"E2.left"),sQuery(id+"F5.wireOp",EDGE,"E2.right")])],"isStart":false});
            var sketch = newSketch(context, id + "F11", { "sketchPlane" : qUnion([Q0])});
            skLineSegment(sketch, "E12.bottom", {"start": v(52.35, -622.88) * mm, "end": v(782.6, -622.88) * mm});
            skLineSegment(sketch, "E12.top", {"start": v(52.35, -45.03) * mm, "end": v(782.6, -45.03) * mm});
            skLineSegment(sketch, "E12.left", {"start": v(52.35, -622.88) * mm, "end": v(52.35, -45.03) * mm});
            skLineSegment(sketch, "E12.right", {"start": v(782.6, -622.88) * mm, "end": v(782.6, -45.03) * mm});
            skSolve(sketch);
        }
        {
            var Q0;
            Q0=makeQuery(id+"F6.opExtrude","CAP_FACE",FACE,{"disambiguationData":[OSD([sQuery(id+"F5.wireOp",EDGE,"E2.bottom"),sQuery(id+"F5.wireOp",EDGE,"E2.top"),sQuery(id+"F5.wireOp",EDGE,"E2.left"),sQuery(id+"F5.wireOp",EDGE,"E2.right")])],"isStart":false});
            var sketch = newSketch(context, id + "F12", { "sketchPlane" : qUnion([Q0])});
            skLineSegment(sketch, "E13.bottom", {"start": v(745.49, -82.55) * mm, "end": v(85.09, -82.55) * mm});
            skLineSegment(sketch, "E13.top", {"start": v(745.49, -590.55) * mm, "end": v(85.09, -590.55) * mm});
            skLineSegment(sketch, "E13.left", {"start": v(745.49, -82.55) * mm, "end": v(745.49, -590.55) * mm});
            skLineSegment(sketch, "E13.right", {"start": v(85.09, -82.55) * mm, "end": v(85.09, -590.55) * mm});
            skPoint(sketch, "E13.middle", {"position": v(415.29, -336.55) * mm});
            skPoint(sketch, "E13.middle.positionSnap0", {"position": v(415.29, -69.85) * mm});
            skPoint(sketch, "E13.middle.positionSnap1", {"position": v(72.39, -336.55) * mm});
            skPoint(sketch, "E13.centerSnap0", {"position": v(415.29, -69.85) * mm});
            skPoint(sketch, "E13.centerSnap1", {"position": v(72.39, -336.55) * mm});
            skSolve(sketch);
        }
        {
            var Q0;
            Q0 = qSketchRegion(id + "F12", true);
            extrude(context, id + "F13", {"entities" : qUnion([Q0]), "operationType" : NewBodyOperationType.REMOVE, "oppositeDirection" : true, "depth" : 152.4 * mm});
        }
        {
            var Q0;
            Q0 = qSketchRegion(id + "F11", true);
            extrude(context, id + "F14", {"entities" : qUnion([Q0]), "operationType" : NewBodyOperationType.ADD, "depth" : 6.35 * mm});
        }
        {
            var Q0;
            Q0=makeQuery(id+"F14.opExtrude","CAP_EDGE",EDGE,{"disambiguationData":[OSD([sQuery(id+"F11.wireOp",EDGE,"E12.right")])],"isStart":false});
            var Q1;
            Q1=makeQuery(id+"F14.opExtrude","CAP_EDGE",EDGE,{"disambiguationData":[OSD([sQuery(id+"F11.wireOp",EDGE,"E12.bottom")])],"isStart":false});
            var Q2;
            Q2=makeQuery(id+"F14.opExtrude","CAP_EDGE",EDGE,{"disambiguationData":[OSD([sQuery(id+"F11.wireOp",EDGE,"E12.left")])],"isStart":false});
            var Q3;
            Q3=makeQuery(id+"F14.opExtrude","CAP_EDGE",EDGE,{"disambiguationData":[OSD([sQuery(id+"F11.wireOp",EDGE,"E12.top")])],"isStart":false});
            var Q4;
            Q4=makeQuery(id+"F14.opExtrude","SWEPT_EDGE",EDGE,{"disambiguationData":[OSD([sQuery(id+"F11.wireOp",EDGE,"E12.bottom"),sQuery(id+"F11.wireOp",EDGE,"E12.right")])]});
            var Q5;
            Q5=makeQuery(id+"F14.opExtrude","SWEPT_EDGE",EDGE,{"disambiguationData":[OSD([sQuery(id+"F11.wireOp",EDGE,"E12.bottom"),sQuery(id+"F11.wireOp",EDGE,"E12.left")])]});
            var Q6;
            Q6=makeQuery(id+"F14.opExtrude","SWEPT_EDGE",EDGE,{"disambiguationData":[OSD([sQuery(id+"F11.wireOp",EDGE,"E12.top"),sQuery(id+"F11.wireOp",EDGE,"E12.right")])]});
            var Q7;
            Q7=makeQuery(id+"F14.opExtrude","SWEPT_EDGE",EDGE,{"disambiguationData":[OSD([sQuery(id+"F11.wireOp",EDGE,"E12.top"),sQuery(id+"F11.wireOp",EDGE,"E12.left")])]});
            fillet(context, id + "F15", {"entities" : qUnion([Q0, Q1, Q2, Q3, Q4, Q5, Q6, Q7]), "radius" : 5.08 * mm, "tangentPropagation" : true, "allowEdgeOverflow" : false});
        }
        {
            var Q0;
            Q0=makeQuery(id+"F1.opExtrude","SWEPT_FACE",FACE,{"disambiguationData":[OSD([sQuery(id+"F0.wireOp",EDGE,"E0.bottom")])]});
            shell(context, id + "F16", {"entities" : qUnion([Q0]), "thickness" : 6.35 * mm});
        }
        {
            var Q0;
            Q0=makeQuery(id+"F3.opExtrude","CAP_FACE",FACE,{"disambiguationData":[OSD([sQuery(id+"F2.wireOp",EDGE,"E1.bottom"),sQuery(id+"F2.wireOp",EDGE,"E1.top"),sQuery(id+"F2.wireOp",EDGE,"E1.left"),sQuery(id+"F2.wireOp",EDGE,"E1.right")])],"isStart":false});
            var sketch = newSketch(context, id + "F17", { "sketchPlane" : qUnion([Q0])});
            skLineSegment(sketch, "E14.bottom", {"start": v(106.54, 109.67) * mm, "end": v(741.54, 109.67) * mm});
            skLineSegment(sketch, "E14.top", {"start": v(106.54, 554.17) * mm, "end": v(741.54, 554.17) * mm});
            skLineSegment(sketch, "E14.left", {"start": v(106.54, 109.67) * mm, "end": v(106.54, 554.17) * mm});
            skLineSegment(sketch, "E14.right", {"start": v(741.54, 109.67) * mm, "end": v(741.54, 554.17) * mm});
            skLineSegment(sketch, "E15.bottom", {"start": v(741.54, 656.23) * mm, "end": v(547.99, 656.23) * mm});
            skLineSegment(sketch, "E15.top", {"start": v(741.54, 1108.19) * mm, "end": v(547.99, 1108.19) * mm});
            skLineSegment(sketch, "E15.left", {"start": v(741.54, 656.23) * mm, "end": v(741.54, 1108.19) * mm});
            skLineSegment(sketch, "E15.right", {"start": v(547.99, 656.23) * mm, "end": v(547.99, 1108.19) * mm});
            skSolve(sketch);
        }
        {
            var Q0;
            Q0 = qSketchRegion(id + "F17", true);
            extrude(context, id + "F18", {"entities" : qUnion([Q0]), "operationType" : NewBodyOperationType.ADD, "depth" : 19.05 * mm});
        }
        {
            var Q0;
            Q0=makeQuery(id+"F18.opExtrude","CAP_FACE",FACE,{"disambiguationData":[OSD([sQuery(id+"F17.wireOp",EDGE,"E14.bottom"),sQuery(id+"F17.wireOp",EDGE,"E14.top"),sQuery(id+"F17.wireOp",EDGE,"E14.left"),sQuery(id+"F17.wireOp",EDGE,"E14.right")])],"isStart":false});
            var sketch = newSketch(context, id + "F19", { "sketchPlane" : qUnion([Q0])});
            skLineSegment(sketch, "E16.bottom", {"start": v(138.13, 528.25) * mm, "end": v(233.38, 528.25) * mm});
            skLineSegment(sketch, "E16.top", {"start": v(138.13, 515.55) * mm, "end": v(233.38, 515.55) * mm});
            skArc(sketch, "E17", {"start": v(233.38, 515.55) * mm, "mid": v(239.73, 521.9) * mm, "end": v(233.38, 528.25) * mm});
            skArc(sketch, "E18", {"start": v(138.13, 528.25) * mm, "mid": v(131.78, 521.9) * mm, "end": v(138.13, 515.55) * mm});
            skLineSegment(sketch, "E19.1.0.0", {"start": v(258.78, 528.32) * mm, "end": v(354.03, 528.32) * mm});
            skArc(sketch, "E19.1.0.1", {"start": v(258.78, 528.32) * mm, "mid": v(252.43, 521.97) * mm, "end": v(258.78, 515.62) * mm});
            skLineSegment(sketch, "E19.1.0.2", {"start": v(258.78, 515.62) * mm, "end": v(354.03, 515.62) * mm});
            skArc(sketch, "E19.1.0.3", {"start": v(354.03, 515.62) * mm, "mid": v(360.38, 521.97) * mm, "end": v(354.03, 528.32) * mm});
            skLineSegment(sketch, "E19.2.0.0", {"start": v(379.43, 528.4) * mm, "end": v(474.68, 528.4) * mm});
            skArc(sketch, "E19.2.0.1", {"start": v(379.43, 528.4) * mm, "mid": v(373.08, 522.05) * mm, "end": v(379.43, 515.7) * mm});
            skLineSegment(sketch, "E19.2.0.2", {"start": v(379.43, 515.7) * mm, "end": v(474.68, 515.7) * mm});
            skArc(sketch, "E19.2.0.3", {"start": v(474.68, 515.7) * mm, "mid": v(481.03, 522.05) * mm, "end": v(474.68, 528.4) * mm});
            skLineSegment(sketch, "E19.3.0.0", {"start": v(500.08, 528.48) * mm, "end": v(595.33, 528.48) * mm});
            skArc(sketch, "E19.3.0.1", {"start": v(500.08, 528.48) * mm, "mid": v(493.73, 522.13) * mm, "end": v(500.08, 515.78) * mm});
            skLineSegment(sketch, "E19.3.0.2", {"start": v(500.08, 515.78) * mm, "end": v(595.33, 515.78) * mm});
            skArc(sketch, "E19.3.0.3", {"start": v(595.33, 515.78) * mm, "mid": v(601.68, 522.13) * mm, "end": v(595.33, 528.48) * mm});
            skLineSegment(sketch, "E19.4.0.0", {"start": v(620.73, 528.55) * mm, "end": v(715.98, 528.55) * mm});
            skArc(sketch, "E19.4.0.1", {"start": v(620.73, 528.55) * mm, "mid": v(614.38, 522.2) * mm, "end": v(620.73, 515.85) * mm});
            skLineSegment(sketch, "E19.4.0.2", {"start": v(620.73, 515.85) * mm, "end": v(715.98, 515.85) * mm});
            skArc(sketch, "E19.4.0.3", {"start": v(715.98, 515.85) * mm, "mid": v(722.33, 522.2) * mm, "end": v(715.98, 528.55) * mm});
            skLineSegment(sketch, "E20.1.0.0", {"start": v(500, 503.08) * mm, "end": v(595.24, 503.08) * mm});
            skLineSegment(sketch, "E20.1.0.1", {"start": v(620.64, 503.15) * mm, "end": v(715.9, 503.15) * mm});
            skLineSegment(sketch, "E20.1.0.2", {"start": v(258.7, 490.22) * mm, "end": v(353.94, 490.22) * mm});
            skLineSegment(sketch, "E20.1.0.3", {"start": v(258.7, 502.92) * mm, "end": v(353.94, 502.92) * mm});
            skArc(sketch, "E20.1.0.4", {"start": v(595.24, 490.38) * mm, "mid": v(601.6, 496.73) * mm, "end": v(595.24, 503.08) * mm});
            skLineSegment(sketch, "E20.1.0.5", {"start": v(379.34, 503) * mm, "end": v(474.6, 503) * mm});
            skLineSegment(sketch, "E20.1.0.6", {"start": v(620.64, 490.45) * mm, "end": v(715.9, 490.45) * mm});
            skLineSegment(sketch, "E20.1.0.8", {"start": v(500, 490.38) * mm, "end": v(595.24, 490.38) * mm});
            skLineSegment(sketch, "E20.1.0.9", {"start": v(138.04, 502.85) * mm, "end": v(233.3, 502.85) * mm});
            skLineSegment(sketch, "E20.1.0.10", {"start": v(379.34, 490.3) * mm, "end": v(474.6, 490.3) * mm});
            skLineSegment(sketch, "E20.1.0.11", {"start": v(138.04, 490.15) * mm, "end": v(233.3, 490.15) * mm});
            skArc(sketch, "E20.1.0.12", {"start": v(379.34, 503) * mm, "mid": v(373, 496.65) * mm, "end": v(379.34, 490.3) * mm});
            skArc(sketch, "E20.1.0.13", {"start": v(715.9, 490.45) * mm, "mid": v(722.24, 496.8) * mm, "end": v(715.9, 503.15) * mm});
            skArc(sketch, "E20.1.0.14", {"start": v(474.6, 490.3) * mm, "mid": v(480.94, 496.65) * mm, "end": v(474.6, 503) * mm});
            skArc(sketch, "E20.1.0.15", {"start": v(353.94, 490.22) * mm, "mid": v(360.3, 496.57) * mm, "end": v(353.94, 502.92) * mm});
            skArc(sketch, "E20.1.0.16", {"start": v(258.7, 502.92) * mm, "mid": v(252.34, 496.57) * mm, "end": v(258.7, 490.22) * mm});
            skArc(sketch, "E20.1.0.17", {"start": v(500, 503.08) * mm, "mid": v(493.64, 496.73) * mm, "end": v(500, 490.38) * mm});
            skArc(sketch, "E20.1.0.18", {"start": v(620.64, 503.15) * mm, "mid": v(614.3, 496.8) * mm, "end": v(620.64, 490.45) * mm});
            skArc(sketch, "E20.1.0.19", {"start": v(233.3, 490.15) * mm, "mid": v(239.64, 496.5) * mm, "end": v(233.3, 502.85) * mm});
            skArc(sketch, "E20.1.0.20", {"start": v(138.04, 502.85) * mm, "mid": v(131.7, 496.5) * mm, "end": v(138.04, 490.15) * mm});
            skLineSegment(sketch, "E20.2.0.0", {"start": v(499.9, 477.68) * mm, "end": v(595.15, 477.68) * mm});
            skLineSegment(sketch, "E20.2.0.1", {"start": v(620.55, 477.75) * mm, "end": v(715.8, 477.75) * mm});
            skLineSegment(sketch, "E20.2.0.2", {"start": v(258.6, 464.82) * mm, "end": v(353.85, 464.82) * mm});
            skLineSegment(sketch, "E20.2.0.3", {"start": v(258.6, 477.52) * mm, "end": v(353.85, 477.52) * mm});
            skArc(sketch, "E20.2.0.4", {"start": v(595.15, 464.98) * mm, "mid": v(601.5, 471.33) * mm, "end": v(595.15, 477.68) * mm});
            skLineSegment(sketch, "E20.2.0.5", {"start": v(379.25, 477.6) * mm, "end": v(474.5, 477.6) * mm});
            skLineSegment(sketch, "E20.2.0.6", {"start": v(620.55, 465.05) * mm, "end": v(715.8, 465.05) * mm});
            skLineSegment(sketch, "E20.2.0.8", {"start": v(499.9, 464.98) * mm, "end": v(595.15, 464.98) * mm});
            skLineSegment(sketch, "E20.2.0.9", {"start": v(137.95, 477.45) * mm, "end": v(233.2, 477.45) * mm});
            skLineSegment(sketch, "E20.2.0.10", {"start": v(379.25, 464.9) * mm, "end": v(474.5, 464.9) * mm});
            skLineSegment(sketch, "E20.2.0.11", {"start": v(137.95, 464.75) * mm, "end": v(233.2, 464.75) * mm});
            skArc(sketch, "E20.2.0.12", {"start": v(379.25, 477.6) * mm, "mid": v(372.9, 471.25) * mm, "end": v(379.25, 464.9) * mm});
            skArc(sketch, "E20.2.0.13", {"start": v(715.8, 465.05) * mm, "mid": v(722.15, 471.4) * mm, "end": v(715.8, 477.75) * mm});
            skArc(sketch, "E20.2.0.14", {"start": v(474.5, 464.9) * mm, "mid": v(480.85, 471.25) * mm, "end": v(474.5, 477.6) * mm});
            skArc(sketch, "E20.2.0.15", {"start": v(353.85, 464.82) * mm, "mid": v(360.2, 471.17) * mm, "end": v(353.85, 477.52) * mm});
            skArc(sketch, "E20.2.0.16", {"start": v(258.6, 477.52) * mm, "mid": v(252.25, 471.17) * mm, "end": v(258.6, 464.82) * mm});
            skArc(sketch, "E20.2.0.17", {"start": v(499.9, 477.68) * mm, "mid": v(493.55, 471.33) * mm, "end": v(499.9, 464.98) * mm});
            skArc(sketch, "E20.2.0.18", {"start": v(620.55, 477.75) * mm, "mid": v(614.2, 471.4) * mm, "end": v(620.55, 465.05) * mm});
            skArc(sketch, "E20.2.0.19", {"start": v(233.2, 464.75) * mm, "mid": v(239.55, 471.1) * mm, "end": v(233.2, 477.45) * mm});
            skArc(sketch, "E20.2.0.20", {"start": v(137.95, 477.45) * mm, "mid": v(131.6, 471.1) * mm, "end": v(137.95, 464.75) * mm});
            skLineSegment(sketch, "E20.3.0.0", {"start": v(499.8, 452.28) * mm, "end": v(595.05, 452.28) * mm});
            skLineSegment(sketch, "E20.3.0.1", {"start": v(620.45, 452.35) * mm, "end": v(715.7, 452.35) * mm});
            skLineSegment(sketch, "E20.3.0.2", {"start": v(258.5, 439.42) * mm, "end": v(353.75, 439.42) * mm});
            skLineSegment(sketch, "E20.3.0.3", {"start": v(258.5, 452.12) * mm, "end": v(353.75, 452.12) * mm});
            skArc(sketch, "E20.3.0.4", {"start": v(595.05, 439.58) * mm, "mid": v(601.4, 445.93) * mm, "end": v(595.05, 452.28) * mm});
            skLineSegment(sketch, "E20.3.0.5", {"start": v(379.15, 452.2) * mm, "end": v(474.4, 452.2) * mm});
            skLineSegment(sketch, "E20.3.0.6", {"start": v(620.45, 439.65) * mm, "end": v(715.7, 439.65) * mm});
            skLineSegment(sketch, "E20.3.0.8", {"start": v(499.8, 439.58) * mm, "end": v(595.05, 439.58) * mm});
            skLineSegment(sketch, "E20.3.0.9", {"start": v(137.85, 452.05) * mm, "end": v(233.1, 452.05) * mm});
            skLineSegment(sketch, "E20.3.0.10", {"start": v(379.15, 439.5) * mm, "end": v(474.4, 439.5) * mm});
            skLineSegment(sketch, "E20.3.0.11", {"start": v(137.85, 439.35) * mm, "end": v(233.1, 439.35) * mm});
            skArc(sketch, "E20.3.0.12", {"start": v(379.15, 452.2) * mm, "mid": v(372.8, 445.85) * mm, "end": v(379.15, 439.5) * mm});
            skArc(sketch, "E20.3.0.13", {"start": v(715.7, 439.65) * mm, "mid": v(722.05, 446) * mm, "end": v(715.7, 452.35) * mm});
            skArc(sketch, "E20.3.0.14", {"start": v(474.4, 439.5) * mm, "mid": v(480.75, 445.85) * mm, "end": v(474.4, 452.2) * mm});
            skArc(sketch, "E20.3.0.15", {"start": v(353.75, 439.42) * mm, "mid": v(360.1, 445.77) * mm, "end": v(353.75, 452.12) * mm});
            skArc(sketch, "E20.3.0.16", {"start": v(258.5, 452.12) * mm, "mid": v(252.15, 445.77) * mm, "end": v(258.5, 439.42) * mm});
            skArc(sketch, "E20.3.0.17", {"start": v(499.8, 452.28) * mm, "mid": v(493.45, 445.93) * mm, "end": v(499.8, 439.58) * mm});
            skArc(sketch, "E20.3.0.18", {"start": v(620.45, 452.35) * mm, "mid": v(614.1, 446) * mm, "end": v(620.45, 439.65) * mm});
            skArc(sketch, "E20.3.0.19", {"start": v(233.1, 439.35) * mm, "mid": v(239.45, 445.7) * mm, "end": v(233.1, 452.05) * mm});
            skArc(sketch, "E20.3.0.20", {"start": v(137.85, 452.05) * mm, "mid": v(131.5, 445.7) * mm, "end": v(137.85, 439.35) * mm});
            skLineSegment(sketch, "E20.4.0.0", {"start": v(499.7, 426.88) * mm, "end": v(594.96, 426.88) * mm});
            skLineSegment(sketch, "E20.4.0.1", {"start": v(620.36, 426.96) * mm, "end": v(715.6, 426.96) * mm});
            skLineSegment(sketch, "E20.4.0.2", {"start": v(258.4, 414.02) * mm, "end": v(353.66, 414.02) * mm});
            skLineSegment(sketch, "E20.4.0.3", {"start": v(258.4, 426.72) * mm, "end": v(353.66, 426.72) * mm});
            skArc(sketch, "E20.4.0.4", {"start": v(594.96, 414.18) * mm, "mid": v(601.3, 420.53) * mm, "end": v(594.96, 426.88) * mm});
            skLineSegment(sketch, "E20.4.0.5", {"start": v(379.06, 426.8) * mm, "end": v(474.3, 426.8) * mm});
            skLineSegment(sketch, "E20.4.0.6", {"start": v(620.36, 414.26) * mm, "end": v(715.6, 414.26) * mm});
            skLineSegment(sketch, "E20.4.0.8", {"start": v(499.7, 414.18) * mm, "end": v(594.96, 414.18) * mm});
            skLineSegment(sketch, "E20.4.0.9", {"start": v(137.76, 426.65) * mm, "end": v(233, 426.65) * mm});
            skLineSegment(sketch, "E20.4.0.10", {"start": v(379.06, 414.1) * mm, "end": v(474.3, 414.1) * mm});
            skLineSegment(sketch, "E20.4.0.11", {"start": v(137.76, 413.95) * mm, "end": v(233, 413.95) * mm});
            skArc(sketch, "E20.4.0.12", {"start": v(379.06, 426.8) * mm, "mid": v(372.7, 420.45) * mm, "end": v(379.06, 414.1) * mm});
            skArc(sketch, "E20.4.0.13", {"start": v(715.6, 414.26) * mm, "mid": v(721.96, 420.6) * mm, "end": v(715.6, 426.96) * mm});
            skArc(sketch, "E20.4.0.14", {"start": v(474.3, 414.1) * mm, "mid": v(480.66, 420.45) * mm, "end": v(474.3, 426.8) * mm});
            skArc(sketch, "E20.4.0.15", {"start": v(353.66, 414.02) * mm, "mid": v(360, 420.37) * mm, "end": v(353.66, 426.72) * mm});
            skArc(sketch, "E20.4.0.16", {"start": v(258.4, 426.72) * mm, "mid": v(252.06, 420.37) * mm, "end": v(258.4, 414.02) * mm});
            skArc(sketch, "E20.4.0.17", {"start": v(499.7, 426.88) * mm, "mid": v(493.36, 420.53) * mm, "end": v(499.7, 414.18) * mm});
            skArc(sketch, "E20.4.0.18", {"start": v(620.36, 426.96) * mm, "mid": v(614, 420.6) * mm, "end": v(620.36, 414.26) * mm});
            skArc(sketch, "E20.4.0.19", {"start": v(233, 413.95) * mm, "mid": v(239.36, 420.3) * mm, "end": v(233, 426.65) * mm});
            skArc(sketch, "E20.4.0.20", {"start": v(137.76, 426.65) * mm, "mid": v(131.4, 420.3) * mm, "end": v(137.76, 413.95) * mm});
            skLineSegment(sketch, "E20.5.0.0", {"start": v(499.62, 401.48) * mm, "end": v(594.87, 401.48) * mm});
            skLineSegment(sketch, "E20.5.0.1", {"start": v(620.27, 401.56) * mm, "end": v(715.52, 401.56) * mm});
            skLineSegment(sketch, "E20.5.0.2", {"start": v(258.32, 388.62) * mm, "end": v(353.57, 388.62) * mm});
            skLineSegment(sketch, "E20.5.0.3", {"start": v(258.32, 401.32) * mm, "end": v(353.57, 401.32) * mm});
            skArc(sketch, "E20.5.0.4", {"start": v(594.87, 388.78) * mm, "mid": v(601.22, 395.13) * mm, "end": v(594.87, 401.48) * mm});
            skLineSegment(sketch, "E20.5.0.5", {"start": v(378.97, 401.4) * mm, "end": v(474.22, 401.4) * mm});
            skLineSegment(sketch, "E20.5.0.6", {"start": v(620.27, 388.86) * mm, "end": v(715.52, 388.86) * mm});
            skLineSegment(sketch, "E20.5.0.8", {"start": v(499.62, 388.78) * mm, "end": v(594.87, 388.78) * mm});
            skLineSegment(sketch, "E20.5.0.9", {"start": v(137.67, 401.25) * mm, "end": v(232.92, 401.25) * mm});
            skLineSegment(sketch, "E20.5.0.10", {"start": v(378.97, 388.7) * mm, "end": v(474.22, 388.7) * mm});
            skLineSegment(sketch, "E20.5.0.11", {"start": v(137.67, 388.55) * mm, "end": v(232.92, 388.55) * mm});
            skArc(sketch, "E20.5.0.12", {"start": v(378.97, 401.4) * mm, "mid": v(372.62, 395.05) * mm, "end": v(378.97, 388.7) * mm});
            skArc(sketch, "E20.5.0.13", {"start": v(715.52, 388.86) * mm, "mid": v(721.87, 395.2) * mm, "end": v(715.52, 401.56) * mm});
            skArc(sketch, "E20.5.0.14", {"start": v(474.22, 388.7) * mm, "mid": v(480.57, 395.05) * mm, "end": v(474.22, 401.4) * mm});
            skArc(sketch, "E20.5.0.15", {"start": v(353.57, 388.62) * mm, "mid": v(359.92, 394.97) * mm, "end": v(353.57, 401.32) * mm});
            skArc(sketch, "E20.5.0.16", {"start": v(258.32, 401.32) * mm, "mid": v(251.97, 394.97) * mm, "end": v(258.32, 388.62) * mm});
            skArc(sketch, "E20.5.0.17", {"start": v(499.62, 401.48) * mm, "mid": v(493.27, 395.13) * mm, "end": v(499.62, 388.78) * mm});
            skArc(sketch, "E20.5.0.18", {"start": v(620.27, 401.56) * mm, "mid": v(613.92, 395.2) * mm, "end": v(620.27, 388.86) * mm});
            skArc(sketch, "E20.5.0.19", {"start": v(232.92, 388.55) * mm, "mid": v(239.27, 394.9) * mm, "end": v(232.92, 401.25) * mm});
            skArc(sketch, "E20.5.0.20", {"start": v(137.67, 401.25) * mm, "mid": v(131.32, 394.9) * mm, "end": v(137.67, 388.55) * mm});
            skLineSegment(sketch, "E20.6.0.0", {"start": v(499.52, 376.08) * mm, "end": v(594.77, 376.08) * mm});
            skLineSegment(sketch, "E20.6.0.1", {"start": v(620.17, 376.16) * mm, "end": v(715.42, 376.16) * mm});
            skLineSegment(sketch, "E20.6.0.2", {"start": v(258.22, 363.22) * mm, "end": v(353.47, 363.22) * mm});
            skLineSegment(sketch, "E20.6.0.3", {"start": v(258.22, 375.92) * mm, "end": v(353.47, 375.92) * mm});
            skArc(sketch, "E20.6.0.4", {"start": v(594.77, 363.38) * mm, "mid": v(601.12, 369.73) * mm, "end": v(594.77, 376.08) * mm});
            skLineSegment(sketch, "E20.6.0.5", {"start": v(378.87, 376) * mm, "end": v(474.12, 376) * mm});
            skLineSegment(sketch, "E20.6.0.6", {"start": v(620.17, 363.46) * mm, "end": v(715.42, 363.46) * mm});
            skLineSegment(sketch, "E20.6.0.8", {"start": v(499.52, 363.38) * mm, "end": v(594.77, 363.38) * mm});
            skLineSegment(sketch, "E20.6.0.9", {"start": v(137.57, 375.85) * mm, "end": v(232.82, 375.85) * mm});
            skLineSegment(sketch, "E20.6.0.10", {"start": v(378.87, 363.3) * mm, "end": v(474.12, 363.3) * mm});
            skLineSegment(sketch, "E20.6.0.11", {"start": v(137.57, 363.15) * mm, "end": v(232.82, 363.15) * mm});
            skArc(sketch, "E20.6.0.12", {"start": v(378.87, 376) * mm, "mid": v(372.52, 369.65) * mm, "end": v(378.87, 363.3) * mm});
            skArc(sketch, "E20.6.0.13", {"start": v(715.42, 363.46) * mm, "mid": v(721.77, 369.8) * mm, "end": v(715.42, 376.16) * mm});
            skArc(sketch, "E20.6.0.14", {"start": v(474.12, 363.3) * mm, "mid": v(480.47, 369.65) * mm, "end": v(474.12, 376) * mm});
            skArc(sketch, "E20.6.0.15", {"start": v(353.47, 363.22) * mm, "mid": v(359.82, 369.57) * mm, "end": v(353.47, 375.92) * mm});
            skArc(sketch, "E20.6.0.16", {"start": v(258.22, 375.92) * mm, "mid": v(251.87, 369.57) * mm, "end": v(258.22, 363.22) * mm});
            skArc(sketch, "E20.6.0.17", {"start": v(499.52, 376.08) * mm, "mid": v(493.17, 369.73) * mm, "end": v(499.52, 363.38) * mm});
            skArc(sketch, "E20.6.0.18", {"start": v(620.17, 376.16) * mm, "mid": v(613.82, 369.8) * mm, "end": v(620.17, 363.46) * mm});
            skArc(sketch, "E20.6.0.19", {"start": v(232.82, 363.15) * mm, "mid": v(239.17, 369.5) * mm, "end": v(232.82, 375.85) * mm});
            skArc(sketch, "E20.6.0.20", {"start": v(137.57, 375.85) * mm, "mid": v(131.22, 369.5) * mm, "end": v(137.57, 363.15) * mm});
            skLineSegment(sketch, "E20.7.0.0", {"start": v(499.43, 350.68) * mm, "end": v(594.68, 350.68) * mm});
            skLineSegment(sketch, "E20.7.0.1", {"start": v(620.08, 350.76) * mm, "end": v(715.33, 350.76) * mm});
            skLineSegment(sketch, "E20.7.0.2", {"start": v(258.13, 337.82) * mm, "end": v(353.38, 337.82) * mm});
            skLineSegment(sketch, "E20.7.0.3", {"start": v(258.13, 350.52) * mm, "end": v(353.38, 350.52) * mm});
            skArc(sketch, "E20.7.0.4", {"start": v(594.68, 337.98) * mm, "mid": v(601.03, 344.33) * mm, "end": v(594.68, 350.68) * mm});
            skLineSegment(sketch, "E20.7.0.5", {"start": v(378.78, 350.6) * mm, "end": v(474.03, 350.6) * mm});
            skLineSegment(sketch, "E20.7.0.6", {"start": v(620.08, 338.06) * mm, "end": v(715.33, 338.06) * mm});
            skLineSegment(sketch, "E20.7.0.8", {"start": v(499.43, 337.98) * mm, "end": v(594.68, 337.98) * mm});
            skLineSegment(sketch, "E20.7.0.9", {"start": v(137.48, 350.45) * mm, "end": v(232.73, 350.45) * mm});
            skLineSegment(sketch, "E20.7.0.10", {"start": v(378.78, 337.9) * mm, "end": v(474.03, 337.9) * mm});
            skLineSegment(sketch, "E20.7.0.11", {"start": v(137.48, 337.75) * mm, "end": v(232.73, 337.75) * mm});
            skArc(sketch, "E20.7.0.12", {"start": v(378.78, 350.6) * mm, "mid": v(372.43, 344.25) * mm, "end": v(378.78, 337.9) * mm});
            skArc(sketch, "E20.7.0.13", {"start": v(715.33, 338.06) * mm, "mid": v(721.68, 344.4) * mm, "end": v(715.33, 350.76) * mm});
            skArc(sketch, "E20.7.0.14", {"start": v(474.03, 337.9) * mm, "mid": v(480.38, 344.25) * mm, "end": v(474.03, 350.6) * mm});
            skArc(sketch, "E20.7.0.15", {"start": v(353.38, 337.82) * mm, "mid": v(359.73, 344.17) * mm, "end": v(353.38, 350.52) * mm});
            skArc(sketch, "E20.7.0.16", {"start": v(258.13, 350.52) * mm, "mid": v(251.78, 344.17) * mm, "end": v(258.13, 337.82) * mm});
            skArc(sketch, "E20.7.0.17", {"start": v(499.43, 350.68) * mm, "mid": v(493.08, 344.33) * mm, "end": v(499.43, 337.98) * mm});
            skArc(sketch, "E20.7.0.18", {"start": v(620.08, 350.76) * mm, "mid": v(613.73, 344.4) * mm, "end": v(620.08, 338.06) * mm});
            skArc(sketch, "E20.7.0.19", {"start": v(232.73, 337.75) * mm, "mid": v(239.08, 344.1) * mm, "end": v(232.73, 350.45) * mm});
            skArc(sketch, "E20.7.0.20", {"start": v(137.48, 350.45) * mm, "mid": v(131.13, 344.1) * mm, "end": v(137.48, 337.75) * mm});
            skLineSegment(sketch, "E20.8.0.0", {"start": v(499.33, 325.28) * mm, "end": v(594.58, 325.28) * mm});
            skLineSegment(sketch, "E20.8.0.1", {"start": v(619.98, 325.36) * mm, "end": v(715.23, 325.36) * mm});
            skLineSegment(sketch, "E20.8.0.2", {"start": v(258.03, 312.42) * mm, "end": v(353.28, 312.42) * mm});
            skLineSegment(sketch, "E20.8.0.3", {"start": v(258.03, 325.12) * mm, "end": v(353.28, 325.12) * mm});
            skArc(sketch, "E20.8.0.4", {"start": v(594.58, 312.58) * mm, "mid": v(600.93, 318.93) * mm, "end": v(594.58, 325.28) * mm});
            skLineSegment(sketch, "E20.8.0.5", {"start": v(378.68, 325.2) * mm, "end": v(473.93, 325.2) * mm});
            skLineSegment(sketch, "E20.8.0.6", {"start": v(619.98, 312.66) * mm, "end": v(715.23, 312.66) * mm});
            skLineSegment(sketch, "E20.8.0.8", {"start": v(499.33, 312.58) * mm, "end": v(594.58, 312.58) * mm});
            skLineSegment(sketch, "E20.8.0.9", {"start": v(137.38, 325.05) * mm, "end": v(232.63, 325.05) * mm});
            skLineSegment(sketch, "E20.8.0.10", {"start": v(378.68, 312.5) * mm, "end": v(473.93, 312.5) * mm});
            skLineSegment(sketch, "E20.8.0.11", {"start": v(137.38, 312.35) * mm, "end": v(232.63, 312.35) * mm});
            skArc(sketch, "E20.8.0.12", {"start": v(378.68, 325.2) * mm, "mid": v(372.33, 318.85) * mm, "end": v(378.68, 312.5) * mm});
            skArc(sketch, "E20.8.0.13", {"start": v(715.23, 312.66) * mm, "mid": v(721.58, 319) * mm, "end": v(715.23, 325.36) * mm});
            skArc(sketch, "E20.8.0.14", {"start": v(473.93, 312.5) * mm, "mid": v(480.28, 318.85) * mm, "end": v(473.93, 325.2) * mm});
            skArc(sketch, "E20.8.0.15", {"start": v(353.28, 312.42) * mm, "mid": v(359.63, 318.77) * mm, "end": v(353.28, 325.12) * mm});
            skArc(sketch, "E20.8.0.16", {"start": v(258.03, 325.12) * mm, "mid": v(251.68, 318.77) * mm, "end": v(258.03, 312.42) * mm});
            skArc(sketch, "E20.8.0.17", {"start": v(499.33, 325.28) * mm, "mid": v(492.98, 318.93) * mm, "end": v(499.33, 312.58) * mm});
            skArc(sketch, "E20.8.0.18", {"start": v(619.98, 325.36) * mm, "mid": v(613.63, 319) * mm, "end": v(619.98, 312.66) * mm});
            skArc(sketch, "E20.8.0.19", {"start": v(232.63, 312.35) * mm, "mid": v(238.98, 318.7) * mm, "end": v(232.63, 325.05) * mm});
            skArc(sketch, "E20.8.0.20", {"start": v(137.38, 325.05) * mm, "mid": v(131.03, 318.7) * mm, "end": v(137.38, 312.35) * mm});
            skLineSegment(sketch, "E20.9.0.0", {"start": v(499.24, 299.88) * mm, "end": v(594.5, 299.88) * mm});
            skLineSegment(sketch, "E20.9.0.1", {"start": v(619.9, 299.96) * mm, "end": v(715.14, 299.96) * mm});
            skLineSegment(sketch, "E20.9.0.2", {"start": v(257.94, 287.02) * mm, "end": v(353.2, 287.02) * mm});
            skLineSegment(sketch, "E20.9.0.3", {"start": v(257.94, 299.72) * mm, "end": v(353.2, 299.72) * mm});
            skArc(sketch, "E20.9.0.4", {"start": v(594.5, 287.18) * mm, "mid": v(600.84, 293.53) * mm, "end": v(594.5, 299.88) * mm});
            skLineSegment(sketch, "E20.9.0.5", {"start": v(378.6, 299.8) * mm, "end": v(473.84, 299.8) * mm});
            skLineSegment(sketch, "E20.9.0.6", {"start": v(619.9, 287.26) * mm, "end": v(715.14, 287.26) * mm});
            skLineSegment(sketch, "E20.9.0.8", {"start": v(499.24, 287.18) * mm, "end": v(594.5, 287.18) * mm});
            skLineSegment(sketch, "E20.9.0.9", {"start": v(137.3, 299.65) * mm, "end": v(232.54, 299.65) * mm});
            skLineSegment(sketch, "E20.9.0.10", {"start": v(378.6, 287.1) * mm, "end": v(473.84, 287.1) * mm});
            skLineSegment(sketch, "E20.9.0.11", {"start": v(137.3, 286.95) * mm, "end": v(232.54, 286.95) * mm});
            skArc(sketch, "E20.9.0.12", {"start": v(378.6, 299.8) * mm, "mid": v(372.24, 293.45) * mm, "end": v(378.6, 287.1) * mm});
            skArc(sketch, "E20.9.0.13", {"start": v(715.14, 287.26) * mm, "mid": v(721.5, 293.6) * mm, "end": v(715.14, 299.96) * mm});
            skArc(sketch, "E20.9.0.14", {"start": v(473.84, 287.1) * mm, "mid": v(480.2, 293.45) * mm, "end": v(473.84, 299.8) * mm});
            skArc(sketch, "E20.9.0.15", {"start": v(353.2, 287.02) * mm, "mid": v(359.54, 293.37) * mm, "end": v(353.2, 299.72) * mm});
            skArc(sketch, "E20.9.0.16", {"start": v(257.94, 299.72) * mm, "mid": v(251.6, 293.37) * mm, "end": v(257.94, 287.02) * mm});
            skArc(sketch, "E20.9.0.17", {"start": v(499.24, 299.88) * mm, "mid": v(492.9, 293.53) * mm, "end": v(499.24, 287.18) * mm});
            skArc(sketch, "E20.9.0.18", {"start": v(619.9, 299.96) * mm, "mid": v(613.54, 293.6) * mm, "end": v(619.9, 287.26) * mm});
            skArc(sketch, "E20.9.0.19", {"start": v(232.54, 286.95) * mm, "mid": v(238.9, 293.3) * mm, "end": v(232.54, 299.65) * mm});
            skArc(sketch, "E20.9.0.20", {"start": v(137.3, 299.65) * mm, "mid": v(130.94, 293.3) * mm, "end": v(137.3, 286.95) * mm});
            skLineSegment(sketch, "E20.10.0.0", {"start": v(499.15, 274.48) * mm, "end": v(594.4, 274.48) * mm});
            skLineSegment(sketch, "E20.10.0.1", {"start": v(619.8, 274.56) * mm, "end": v(715.05, 274.56) * mm});
            skLineSegment(sketch, "E20.10.0.2", {"start": v(257.85, 261.62) * mm, "end": v(353.1, 261.62) * mm});
            skLineSegment(sketch, "E20.10.0.3", {"start": v(257.85, 274.32) * mm, "end": v(353.1, 274.32) * mm});
            skArc(sketch, "E20.10.0.4", {"start": v(594.4, 261.78) * mm, "mid": v(600.75, 268.13) * mm, "end": v(594.4, 274.48) * mm});
            skLineSegment(sketch, "E20.10.0.5", {"start": v(378.5, 274.4) * mm, "end": v(473.75, 274.4) * mm});
            skLineSegment(sketch, "E20.10.0.6", {"start": v(619.8, 261.86) * mm, "end": v(715.05, 261.86) * mm});
            skLineSegment(sketch, "E20.10.0.8", {"start": v(499.15, 261.78) * mm, "end": v(594.4, 261.78) * mm});
            skLineSegment(sketch, "E20.10.0.9", {"start": v(137.2, 274.25) * mm, "end": v(232.45, 274.25) * mm});
            skLineSegment(sketch, "E20.10.0.10", {"start": v(378.5, 261.7) * mm, "end": v(473.75, 261.7) * mm});
            skLineSegment(sketch, "E20.10.0.11", {"start": v(137.2, 261.55) * mm, "end": v(232.45, 261.55) * mm});
            skArc(sketch, "E20.10.0.12", {"start": v(378.5, 274.4) * mm, "mid": v(372.15, 268.05) * mm, "end": v(378.5, 261.7) * mm});
            skArc(sketch, "E20.10.0.13", {"start": v(715.05, 261.86) * mm, "mid": v(721.4, 268.2) * mm, "end": v(715.05, 274.56) * mm});
            skArc(sketch, "E20.10.0.14", {"start": v(473.75, 261.7) * mm, "mid": v(480.1, 268.05) * mm, "end": v(473.75, 274.4) * mm});
            skArc(sketch, "E20.10.0.15", {"start": v(353.1, 261.62) * mm, "mid": v(359.45, 267.97) * mm, "end": v(353.1, 274.32) * mm});
            skArc(sketch, "E20.10.0.16", {"start": v(257.85, 274.32) * mm, "mid": v(251.5, 267.97) * mm, "end": v(257.85, 261.62) * mm});
            skArc(sketch, "E20.10.0.17", {"start": v(499.15, 274.48) * mm, "mid": v(492.8, 268.13) * mm, "end": v(499.15, 261.78) * mm});
            skArc(sketch, "E20.10.0.18", {"start": v(619.8, 274.56) * mm, "mid": v(613.45, 268.2) * mm, "end": v(619.8, 261.86) * mm});
            skArc(sketch, "E20.10.0.19", {"start": v(232.45, 261.55) * mm, "mid": v(238.8, 267.9) * mm, "end": v(232.45, 274.25) * mm});
            skArc(sketch, "E20.10.0.20", {"start": v(137.2, 274.25) * mm, "mid": v(130.85, 267.9) * mm, "end": v(137.2, 261.55) * mm});
            skLineSegment(sketch, "E20.11.0.0", {"start": v(499.05, 249.08) * mm, "end": v(594.3, 249.08) * mm});
            skLineSegment(sketch, "E20.11.0.1", {"start": v(619.7, 249.16) * mm, "end": v(714.95, 249.16) * mm});
            skLineSegment(sketch, "E20.11.0.2", {"start": v(257.75, 236.22) * mm, "end": v(353, 236.22) * mm});
            skLineSegment(sketch, "E20.11.0.3", {"start": v(257.75, 248.92) * mm, "end": v(353, 248.92) * mm});
            skArc(sketch, "E20.11.0.4", {"start": v(594.3, 236.38) * mm, "mid": v(600.65, 242.73) * mm, "end": v(594.3, 249.08) * mm});
            skLineSegment(sketch, "E20.11.0.5", {"start": v(378.4, 249) * mm, "end": v(473.65, 249) * mm});
            skLineSegment(sketch, "E20.11.0.6", {"start": v(619.7, 236.46) * mm, "end": v(714.95, 236.46) * mm});
            skLineSegment(sketch, "E20.11.0.8", {"start": v(499.05, 236.38) * mm, "end": v(594.3, 236.38) * mm});
            skLineSegment(sketch, "E20.11.0.9", {"start": v(137.1, 248.85) * mm, "end": v(232.35, 248.85) * mm});
            skLineSegment(sketch, "E20.11.0.10", {"start": v(378.4, 236.3) * mm, "end": v(473.65, 236.3) * mm});
            skLineSegment(sketch, "E20.11.0.11", {"start": v(137.1, 236.15) * mm, "end": v(232.35, 236.15) * mm});
            skArc(sketch, "E20.11.0.12", {"start": v(378.4, 249) * mm, "mid": v(372.05, 242.65) * mm, "end": v(378.4, 236.3) * mm});
            skArc(sketch, "E20.11.0.13", {"start": v(714.95, 236.46) * mm, "mid": v(721.3, 242.8) * mm, "end": v(714.95, 249.16) * mm});
            skArc(sketch, "E20.11.0.14", {"start": v(473.65, 236.3) * mm, "mid": v(480, 242.65) * mm, "end": v(473.65, 249) * mm});
            skArc(sketch, "E20.11.0.15", {"start": v(353, 236.22) * mm, "mid": v(359.35, 242.57) * mm, "end": v(353, 248.92) * mm});
            skArc(sketch, "E20.11.0.16", {"start": v(257.75, 248.92) * mm, "mid": v(251.4, 242.57) * mm, "end": v(257.75, 236.22) * mm});
            skArc(sketch, "E20.11.0.17", {"start": v(499.05, 249.08) * mm, "mid": v(492.7, 242.73) * mm, "end": v(499.05, 236.38) * mm});
            skArc(sketch, "E20.11.0.18", {"start": v(619.7, 249.16) * mm, "mid": v(613.35, 242.8) * mm, "end": v(619.7, 236.46) * mm});
            skArc(sketch, "E20.11.0.19", {"start": v(232.35, 236.15) * mm, "mid": v(238.7, 242.5) * mm, "end": v(232.35, 248.85) * mm});
            skArc(sketch, "E20.11.0.20", {"start": v(137.1, 248.85) * mm, "mid": v(130.75, 242.5) * mm, "end": v(137.1, 236.15) * mm});
            skLineSegment(sketch, "E20.12.0.0", {"start": v(498.96, 223.68) * mm, "end": v(594.2, 223.68) * mm});
            skLineSegment(sketch, "E20.12.0.1", {"start": v(619.6, 223.76) * mm, "end": v(714.86, 223.76) * mm});
            skLineSegment(sketch, "E20.12.0.2", {"start": v(257.66, 210.83) * mm, "end": v(352.9, 210.83) * mm});
            skLineSegment(sketch, "E20.12.0.3", {"start": v(257.66, 223.53) * mm, "end": v(352.9, 223.53) * mm});
            skArc(sketch, "E20.12.0.4", {"start": v(594.2, 210.98) * mm, "mid": v(600.56, 217.33) * mm, "end": v(594.2, 223.68) * mm});
            skLineSegment(sketch, "E20.12.0.5", {"start": v(378.3, 223.6) * mm, "end": v(473.56, 223.6) * mm});
            skLineSegment(sketch, "E20.12.0.6", {"start": v(619.6, 211.06) * mm, "end": v(714.86, 211.06) * mm});
            skLineSegment(sketch, "E20.12.0.8", {"start": v(498.96, 210.98) * mm, "end": v(594.2, 210.98) * mm});
            skLineSegment(sketch, "E20.12.0.9", {"start": v(137, 223.45) * mm, "end": v(232.26, 223.45) * mm});
            skLineSegment(sketch, "E20.12.0.10", {"start": v(378.3, 210.9) * mm, "end": v(473.56, 210.9) * mm});
            skLineSegment(sketch, "E20.12.0.11", {"start": v(137, 210.75) * mm, "end": v(232.26, 210.75) * mm});
            skArc(sketch, "E20.12.0.12", {"start": v(378.3, 223.6) * mm, "mid": v(371.96, 217.25) * mm, "end": v(378.3, 210.9) * mm});
            skArc(sketch, "E20.12.0.13", {"start": v(714.86, 211.06) * mm, "mid": v(721.2, 217.4) * mm, "end": v(714.86, 223.76) * mm});
            skArc(sketch, "E20.12.0.14", {"start": v(473.56, 210.9) * mm, "mid": v(479.9, 217.25) * mm, "end": v(473.56, 223.6) * mm});
            skArc(sketch, "E20.12.0.15", {"start": v(352.9, 210.83) * mm, "mid": v(359.26, 217.18) * mm, "end": v(352.9, 223.53) * mm});
            skArc(sketch, "E20.12.0.16", {"start": v(257.66, 223.53) * mm, "mid": v(251.3, 217.18) * mm, "end": v(257.66, 210.83) * mm});
            skArc(sketch, "E20.12.0.17", {"start": v(498.96, 223.68) * mm, "mid": v(492.6, 217.33) * mm, "end": v(498.96, 210.98) * mm});
            skArc(sketch, "E20.12.0.18", {"start": v(619.6, 223.76) * mm, "mid": v(613.26, 217.4) * mm, "end": v(619.6, 211.06) * mm});
            skArc(sketch, "E20.12.0.19", {"start": v(232.26, 210.75) * mm, "mid": v(238.6, 217.1) * mm, "end": v(232.26, 223.45) * mm});
            skArc(sketch, "E20.12.0.20", {"start": v(137, 223.45) * mm, "mid": v(130.66, 217.1) * mm, "end": v(137, 210.75) * mm});
            skLineSegment(sketch, "E20.13.0.0", {"start": v(498.87, 198.28) * mm, "end": v(594.12, 198.28) * mm});
            skLineSegment(sketch, "E20.13.0.1", {"start": v(619.52, 198.36) * mm, "end": v(714.77, 198.36) * mm});
            skLineSegment(sketch, "E20.13.0.2", {"start": v(257.57, 185.43) * mm, "end": v(352.82, 185.43) * mm});
            skLineSegment(sketch, "E20.13.0.3", {"start": v(257.57, 198.13) * mm, "end": v(352.82, 198.13) * mm});
            skArc(sketch, "E20.13.0.4", {"start": v(594.12, 185.58) * mm, "mid": v(600.47, 191.93) * mm, "end": v(594.12, 198.28) * mm});
            skLineSegment(sketch, "E20.13.0.5", {"start": v(378.22, 198.2) * mm, "end": v(473.47, 198.2) * mm});
            skLineSegment(sketch, "E20.13.0.6", {"start": v(619.52, 185.66) * mm, "end": v(714.77, 185.66) * mm});
            skLineSegment(sketch, "E20.13.0.8", {"start": v(498.87, 185.58) * mm, "end": v(594.12, 185.58) * mm});
            skLineSegment(sketch, "E20.13.0.9", {"start": v(136.92, 198.05) * mm, "end": v(232.17, 198.05) * mm});
            skLineSegment(sketch, "E20.13.0.10", {"start": v(378.22, 185.5) * mm, "end": v(473.47, 185.5) * mm});
            skLineSegment(sketch, "E20.13.0.11", {"start": v(136.92, 185.35) * mm, "end": v(232.17, 185.35) * mm});
            skArc(sketch, "E20.13.0.12", {"start": v(378.22, 198.2) * mm, "mid": v(371.87, 191.85) * mm, "end": v(378.22, 185.5) * mm});
            skArc(sketch, "E20.13.0.13", {"start": v(714.77, 185.66) * mm, "mid": v(721.12, 192) * mm, "end": v(714.77, 198.36) * mm});
            skArc(sketch, "E20.13.0.14", {"start": v(473.47, 185.5) * mm, "mid": v(479.82, 191.85) * mm, "end": v(473.47, 198.2) * mm});
            skArc(sketch, "E20.13.0.15", {"start": v(352.82, 185.43) * mm, "mid": v(359.17, 191.78) * mm, "end": v(352.82, 198.13) * mm});
            skArc(sketch, "E20.13.0.16", {"start": v(257.57, 198.13) * mm, "mid": v(251.22, 191.78) * mm, "end": v(257.57, 185.43) * mm});
            skArc(sketch, "E20.13.0.17", {"start": v(498.87, 198.28) * mm, "mid": v(492.52, 191.93) * mm, "end": v(498.87, 185.58) * mm});
            skArc(sketch, "E20.13.0.18", {"start": v(619.52, 198.36) * mm, "mid": v(613.17, 192) * mm, "end": v(619.52, 185.66) * mm});
            skArc(sketch, "E20.13.0.19", {"start": v(232.17, 185.35) * mm, "mid": v(238.52, 191.7) * mm, "end": v(232.17, 198.05) * mm});
            skArc(sketch, "E20.13.0.20", {"start": v(136.92, 198.05) * mm, "mid": v(130.57, 191.7) * mm, "end": v(136.92, 185.35) * mm});
            skLineSegment(sketch, "E20.14.0.0", {"start": v(498.77, 172.88) * mm, "end": v(594.02, 172.88) * mm});
            skLineSegment(sketch, "E20.14.0.1", {"start": v(619.42, 172.96) * mm, "end": v(714.67, 172.96) * mm});
            skLineSegment(sketch, "E20.14.0.2", {"start": v(257.47, 160.03) * mm, "end": v(352.72, 160.03) * mm});
            skLineSegment(sketch, "E20.14.0.3", {"start": v(257.47, 172.73) * mm, "end": v(352.72, 172.73) * mm});
            skArc(sketch, "E20.14.0.4", {"start": v(594.02, 160.18) * mm, "mid": v(600.37, 166.53) * mm, "end": v(594.02, 172.88) * mm});
            skLineSegment(sketch, "E20.14.0.5", {"start": v(378.12, 172.8) * mm, "end": v(473.37, 172.8) * mm});
            skLineSegment(sketch, "E20.14.0.6", {"start": v(619.42, 160.26) * mm, "end": v(714.67, 160.26) * mm});
            skLineSegment(sketch, "E20.14.0.8", {"start": v(498.77, 160.18) * mm, "end": v(594.02, 160.18) * mm});
            skLineSegment(sketch, "E20.14.0.9", {"start": v(136.82, 172.65) * mm, "end": v(232.07, 172.65) * mm});
            skLineSegment(sketch, "E20.14.0.10", {"start": v(378.12, 160.1) * mm, "end": v(473.37, 160.1) * mm});
            skLineSegment(sketch, "E20.14.0.11", {"start": v(136.82, 159.95) * mm, "end": v(232.07, 159.95) * mm});
            skArc(sketch, "E20.14.0.12", {"start": v(378.12, 172.8) * mm, "mid": v(371.77, 166.45) * mm, "end": v(378.12, 160.1) * mm});
            skArc(sketch, "E20.14.0.13", {"start": v(714.67, 160.26) * mm, "mid": v(721.02, 166.6) * mm, "end": v(714.67, 172.96) * mm});
            skArc(sketch, "E20.14.0.14", {"start": v(473.37, 160.1) * mm, "mid": v(479.72, 166.45) * mm, "end": v(473.37, 172.8) * mm});
            skArc(sketch, "E20.14.0.15", {"start": v(352.72, 160.03) * mm, "mid": v(359.07, 166.38) * mm, "end": v(352.72, 172.73) * mm});
            skArc(sketch, "E20.14.0.16", {"start": v(257.47, 172.73) * mm, "mid": v(251.12, 166.38) * mm, "end": v(257.47, 160.03) * mm});
            skArc(sketch, "E20.14.0.17", {"start": v(498.77, 172.88) * mm, "mid": v(492.42, 166.53) * mm, "end": v(498.77, 160.18) * mm});
            skArc(sketch, "E20.14.0.18", {"start": v(619.42, 172.96) * mm, "mid": v(613.07, 166.6) * mm, "end": v(619.42, 160.26) * mm});
            skArc(sketch, "E20.14.0.19", {"start": v(232.07, 159.95) * mm, "mid": v(238.42, 166.3) * mm, "end": v(232.07, 172.65) * mm});
            skArc(sketch, "E20.14.0.20", {"start": v(136.82, 172.65) * mm, "mid": v(130.47, 166.3) * mm, "end": v(136.82, 159.95) * mm});
            skLineSegment(sketch, "E20.15.0.0", {"start": v(498.68, 147.48) * mm, "end": v(593.93, 147.48) * mm});
            skLineSegment(sketch, "E20.15.0.1", {"start": v(619.33, 147.56) * mm, "end": v(714.58, 147.56) * mm});
            skLineSegment(sketch, "E20.15.0.2", {"start": v(257.38, 134.63) * mm, "end": v(352.63, 134.63) * mm});
            skLineSegment(sketch, "E20.15.0.3", {"start": v(257.38, 147.33) * mm, "end": v(352.63, 147.33) * mm});
            skArc(sketch, "E20.15.0.4", {"start": v(593.93, 134.78) * mm, "mid": v(600.28, 141.13) * mm, "end": v(593.93, 147.48) * mm});
            skLineSegment(sketch, "E20.15.0.5", {"start": v(378.03, 147.4) * mm, "end": v(473.28, 147.4) * mm});
            skLineSegment(sketch, "E20.15.0.6", {"start": v(619.33, 134.86) * mm, "end": v(714.58, 134.86) * mm});
            skLineSegment(sketch, "E20.15.0.8", {"start": v(498.68, 134.78) * mm, "end": v(593.93, 134.78) * mm});
            skLineSegment(sketch, "E20.15.0.9", {"start": v(136.73, 147.25) * mm, "end": v(231.98, 147.25) * mm});
            skLineSegment(sketch, "E20.15.0.10", {"start": v(378.03, 134.7) * mm, "end": v(473.28, 134.7) * mm});
            skLineSegment(sketch, "E20.15.0.11", {"start": v(136.73, 134.55) * mm, "end": v(231.98, 134.55) * mm});
            skArc(sketch, "E20.15.0.12", {"start": v(378.03, 147.4) * mm, "mid": v(371.68, 141.05) * mm, "end": v(378.03, 134.7) * mm});
            skArc(sketch, "E20.15.0.13", {"start": v(714.58, 134.86) * mm, "mid": v(720.93, 141.2) * mm, "end": v(714.58, 147.56) * mm});
            skArc(sketch, "E20.15.0.14", {"start": v(473.28, 134.7) * mm, "mid": v(479.63, 141.05) * mm, "end": v(473.28, 147.4) * mm});
            skArc(sketch, "E20.15.0.15", {"start": v(352.63, 134.63) * mm, "mid": v(358.98, 140.98) * mm, "end": v(352.63, 147.33) * mm});
            skArc(sketch, "E20.15.0.16", {"start": v(257.38, 147.33) * mm, "mid": v(251.03, 140.98) * mm, "end": v(257.38, 134.63) * mm});
            skArc(sketch, "E20.15.0.17", {"start": v(498.68, 147.48) * mm, "mid": v(492.33, 141.13) * mm, "end": v(498.68, 134.78) * mm});
            skArc(sketch, "E20.15.0.18", {"start": v(619.33, 147.56) * mm, "mid": v(612.98, 141.2) * mm, "end": v(619.33, 134.86) * mm});
            skArc(sketch, "E20.15.0.19", {"start": v(231.98, 134.55) * mm, "mid": v(238.33, 140.9) * mm, "end": v(231.98, 147.25) * mm});
            skArc(sketch, "E20.15.0.20", {"start": v(136.73, 147.25) * mm, "mid": v(130.38, 140.9) * mm, "end": v(136.73, 134.55) * mm});
            skLineSegment(sketch, "E20.direction1", {"start": v(138.13, 515.55) * mm, "end": v(138.04, 490.15) * mm, "construction": true});
            skSolve(sketch);
        }
        {
            var Q0;
            Q0 = qSketchRegion(id + "F19", true);
            extrude(context, id + "F20", {"entities" : qUnion([Q0]), "operationType" : NewBodyOperationType.REMOVE, "oppositeDirection" : true, "depth" : 25.4 * mm});
        }
        {
            var Q0;
            Q0=makeQuery(id+"F18.opExtrude","CAP_FACE",FACE,{"disambiguationData":[OSD([sQuery(id+"F17.wireOp",EDGE,"E15.bottom"),sQuery(id+"F17.wireOp",EDGE,"E15.top"),sQuery(id+"F17.wireOp",EDGE,"E15.left"),sQuery(id+"F17.wireOp",EDGE,"E15.right")])],"isStart":false});
            var sketch = newSketch(context, id + "F21", { "sketchPlane" : qUnion([Q0])});
            skLineSegment(sketch, "E21.bottom", {"start": v(560.62, 1083.16) * mm, "end": v(726.6, 1083.16) * mm});
            skLineSegment(sketch, "E21.top", {"start": v(560.62, 1071.63) * mm, "end": v(726.6, 1071.63) * mm});
            skLineSegment(sketch, "E21.left", {"start": v(560.62, 1083.16) * mm, "end": v(560.62, 1071.63) * mm});
            skLineSegment(sketch, "E21.right", {"start": v(726.6, 1083.16) * mm, "end": v(726.6, 1071.63) * mm});
            skLineSegment(sketch, "E22.1.0.0", {"start": v(560.68, 1064.1) * mm, "end": v(726.67, 1064.1) * mm});
            skLineSegment(sketch, "E22.1.0.1", {"start": v(560.68, 1052.58) * mm, "end": v(726.67, 1052.58) * mm});
            skLineSegment(sketch, "E22.1.0.2", {"start": v(560.68, 1064.1) * mm, "end": v(560.68, 1052.58) * mm});
            skLineSegment(sketch, "E22.1.0.3", {"start": v(726.67, 1064.1) * mm, "end": v(726.67, 1052.58) * mm});
            skLineSegment(sketch, "E22.2.0.0", {"start": v(560.74, 1045.06) * mm, "end": v(726.73, 1045.06) * mm});
            skLineSegment(sketch, "E22.2.0.1", {"start": v(560.74, 1033.53) * mm, "end": v(726.73, 1033.53) * mm});
            skLineSegment(sketch, "E22.2.0.2", {"start": v(560.74, 1045.06) * mm, "end": v(560.74, 1033.53) * mm});
            skLineSegment(sketch, "E22.2.0.3", {"start": v(726.73, 1045.06) * mm, "end": v(726.73, 1033.53) * mm});
            skLineSegment(sketch, "E22.3.0.0", {"start": v(560.8, 1026) * mm, "end": v(726.8, 1026) * mm});
            skLineSegment(sketch, "E22.3.0.1", {"start": v(560.8, 1014.48) * mm, "end": v(726.8, 1014.48) * mm});
            skLineSegment(sketch, "E22.3.0.2", {"start": v(560.8, 1026) * mm, "end": v(560.8, 1014.48) * mm});
            skLineSegment(sketch, "E22.3.0.3", {"start": v(726.8, 1026) * mm, "end": v(726.8, 1014.48) * mm});
            skLineSegment(sketch, "E22.4.0.0", {"start": v(560.87, 1006.96) * mm, "end": v(726.85, 1006.96) * mm});
            skLineSegment(sketch, "E22.4.0.1", {"start": v(560.87, 995.43) * mm, "end": v(726.85, 995.43) * mm});
            skLineSegment(sketch, "E22.4.0.2", {"start": v(560.87, 1006.96) * mm, "end": v(560.87, 995.43) * mm});
            skLineSegment(sketch, "E22.4.0.3", {"start": v(726.85, 1006.96) * mm, "end": v(726.85, 995.43) * mm});
            skLineSegment(sketch, "E22.5.0.0", {"start": v(560.93, 987.9) * mm, "end": v(726.92, 987.9) * mm});
            skLineSegment(sketch, "E22.5.0.1", {"start": v(560.93, 976.38) * mm, "end": v(726.92, 976.38) * mm});
            skLineSegment(sketch, "E22.5.0.2", {"start": v(560.93, 987.9) * mm, "end": v(560.93, 976.38) * mm});
            skLineSegment(sketch, "E22.5.0.3", {"start": v(726.92, 987.9) * mm, "end": v(726.92, 976.38) * mm});
            skLineSegment(sketch, "E22.6.0.0", {"start": v(561, 968.86) * mm, "end": v(726.98, 968.86) * mm});
            skLineSegment(sketch, "E22.6.0.1", {"start": v(561, 957.33) * mm, "end": v(726.98, 957.33) * mm});
            skLineSegment(sketch, "E22.6.0.2", {"start": v(561, 968.86) * mm, "end": v(561, 957.33) * mm});
            skLineSegment(sketch, "E22.6.0.3", {"start": v(726.98, 968.86) * mm, "end": v(726.98, 957.33) * mm});
            skLineSegment(sketch, "E22.7.0.0", {"start": v(561.06, 949.8) * mm, "end": v(727.04, 949.8) * mm});
            skLineSegment(sketch, "E22.7.0.1", {"start": v(561.06, 938.28) * mm, "end": v(727.04, 938.28) * mm});
            skLineSegment(sketch, "E22.7.0.2", {"start": v(561.06, 949.8) * mm, "end": v(561.06, 938.28) * mm});
            skLineSegment(sketch, "E22.7.0.3", {"start": v(727.04, 949.8) * mm, "end": v(727.04, 938.28) * mm});
            skLineSegment(sketch, "E22.8.0.0", {"start": v(561.12, 930.76) * mm, "end": v(727.1, 930.76) * mm});
            skLineSegment(sketch, "E22.8.0.1", {"start": v(561.12, 919.23) * mm, "end": v(727.1, 919.23) * mm});
            skLineSegment(sketch, "E22.8.0.2", {"start": v(561.12, 930.76) * mm, "end": v(561.12, 919.23) * mm});
            skLineSegment(sketch, "E22.8.0.3", {"start": v(727.1, 930.76) * mm, "end": v(727.1, 919.23) * mm});
            skLineSegment(sketch, "E22.9.0.0", {"start": v(561.18, 911.7) * mm, "end": v(727.17, 911.7) * mm});
            skLineSegment(sketch, "E22.9.0.1", {"start": v(561.18, 900.18) * mm, "end": v(727.17, 900.18) * mm});
            skLineSegment(sketch, "E22.9.0.2", {"start": v(561.18, 911.7) * mm, "end": v(561.18, 900.18) * mm});
            skLineSegment(sketch, "E22.9.0.3", {"start": v(727.17, 911.7) * mm, "end": v(727.17, 900.18) * mm});
            skLineSegment(sketch, "E22.10.0.0", {"start": v(561.25, 892.66) * mm, "end": v(727.23, 892.66) * mm});
            skLineSegment(sketch, "E22.10.0.1", {"start": v(561.25, 881.13) * mm, "end": v(727.23, 881.13) * mm});
            skLineSegment(sketch, "E22.10.0.2", {"start": v(561.25, 892.66) * mm, "end": v(561.25, 881.13) * mm});
            skLineSegment(sketch, "E22.10.0.3", {"start": v(727.23, 892.66) * mm, "end": v(727.23, 881.13) * mm});
            skLineSegment(sketch, "E22.11.0.0", {"start": v(561.31, 873.6) * mm, "end": v(727.3, 873.6) * mm});
            skLineSegment(sketch, "E22.11.0.1", {"start": v(561.31, 862.08) * mm, "end": v(727.3, 862.08) * mm});
            skLineSegment(sketch, "E22.11.0.2", {"start": v(561.31, 873.6) * mm, "end": v(561.31, 862.08) * mm});
            skLineSegment(sketch, "E22.11.0.3", {"start": v(727.3, 873.6) * mm, "end": v(727.3, 862.08) * mm});
            skLineSegment(sketch, "E22.12.0.0", {"start": v(561.37, 854.56) * mm, "end": v(727.36, 854.56) * mm});
            skLineSegment(sketch, "E22.12.0.1", {"start": v(561.37, 843.03) * mm, "end": v(727.36, 843.03) * mm});
            skLineSegment(sketch, "E22.12.0.2", {"start": v(561.37, 854.56) * mm, "end": v(561.37, 843.03) * mm});
            skLineSegment(sketch, "E22.12.0.3", {"start": v(727.36, 854.56) * mm, "end": v(727.36, 843.03) * mm});
            skLineSegment(sketch, "E22.13.0.0", {"start": v(561.44, 835.5) * mm, "end": v(727.42, 835.5) * mm});
            skLineSegment(sketch, "E22.13.0.1", {"start": v(561.44, 823.98) * mm, "end": v(727.42, 823.98) * mm});
            skLineSegment(sketch, "E22.13.0.2", {"start": v(561.44, 835.5) * mm, "end": v(561.44, 823.98) * mm});
            skLineSegment(sketch, "E22.13.0.3", {"start": v(727.42, 835.5) * mm, "end": v(727.42, 823.98) * mm});
            skLineSegment(sketch, "E22.14.0.0", {"start": v(561.5, 816.46) * mm, "end": v(727.48, 816.46) * mm});
            skLineSegment(sketch, "E22.14.0.1", {"start": v(561.5, 804.93) * mm, "end": v(727.48, 804.93) * mm});
            skLineSegment(sketch, "E22.14.0.2", {"start": v(561.5, 816.46) * mm, "end": v(561.5, 804.93) * mm});
            skLineSegment(sketch, "E22.14.0.3", {"start": v(727.48, 816.46) * mm, "end": v(727.48, 804.93) * mm});
            skLineSegment(sketch, "E22.15.0.0", {"start": v(561.56, 797.4) * mm, "end": v(727.55, 797.4) * mm});
            skLineSegment(sketch, "E22.15.0.1", {"start": v(561.56, 785.88) * mm, "end": v(727.55, 785.88) * mm});
            skLineSegment(sketch, "E22.15.0.2", {"start": v(561.56, 797.4) * mm, "end": v(561.56, 785.88) * mm});
            skLineSegment(sketch, "E22.15.0.3", {"start": v(727.55, 797.4) * mm, "end": v(727.55, 785.88) * mm});
            skLineSegment(sketch, "E22.16.0.0", {"start": v(561.63, 778.36) * mm, "end": v(727.61, 778.36) * mm});
            skLineSegment(sketch, "E22.16.0.1", {"start": v(561.63, 766.83) * mm, "end": v(727.61, 766.83) * mm});
            skLineSegment(sketch, "E22.16.0.2", {"start": v(561.63, 778.36) * mm, "end": v(561.63, 766.83) * mm});
            skLineSegment(sketch, "E22.16.0.3", {"start": v(727.61, 778.36) * mm, "end": v(727.61, 766.83) * mm});
            skLineSegment(sketch, "E22.17.0.0", {"start": v(561.69, 759.3) * mm, "end": v(727.67, 759.3) * mm});
            skLineSegment(sketch, "E22.17.0.1", {"start": v(561.69, 747.78) * mm, "end": v(727.67, 747.78) * mm});
            skLineSegment(sketch, "E22.17.0.2", {"start": v(561.69, 759.3) * mm, "end": v(561.69, 747.78) * mm});
            skLineSegment(sketch, "E22.17.0.3", {"start": v(727.67, 759.3) * mm, "end": v(727.67, 747.78) * mm});
            skLineSegment(sketch, "E22.18.0.0", {"start": v(561.75, 740.26) * mm, "end": v(727.74, 740.26) * mm});
            skLineSegment(sketch, "E22.18.0.1", {"start": v(561.75, 728.73) * mm, "end": v(727.74, 728.73) * mm});
            skLineSegment(sketch, "E22.18.0.2", {"start": v(561.75, 740.26) * mm, "end": v(561.75, 728.73) * mm});
            skLineSegment(sketch, "E22.18.0.3", {"start": v(727.74, 740.26) * mm, "end": v(727.74, 728.73) * mm});
            skLineSegment(sketch, "E22.19.0.0", {"start": v(561.81, 721.2) * mm, "end": v(727.8, 721.2) * mm});
            skLineSegment(sketch, "E22.19.0.1", {"start": v(561.81, 709.68) * mm, "end": v(727.8, 709.68) * mm});
            skLineSegment(sketch, "E22.19.0.2", {"start": v(561.81, 721.2) * mm, "end": v(561.81, 709.68) * mm});
            skLineSegment(sketch, "E22.19.0.3", {"start": v(727.8, 721.2) * mm, "end": v(727.8, 709.68) * mm});
            skLineSegment(sketch, "E22.20.0.0", {"start": v(561.88, 702.16) * mm, "end": v(727.86, 702.16) * mm});
            skLineSegment(sketch, "E22.20.0.1", {"start": v(561.88, 690.63) * mm, "end": v(727.86, 690.63) * mm});
            skLineSegment(sketch, "E22.20.0.2", {"start": v(561.88, 702.16) * mm, "end": v(561.88, 690.63) * mm});
            skLineSegment(sketch, "E22.20.0.3", {"start": v(727.86, 702.16) * mm, "end": v(727.86, 690.63) * mm});
            skLineSegment(sketch, "E22.21.0.0", {"start": v(561.94, 683.1) * mm, "end": v(727.93, 683.1) * mm});
            skLineSegment(sketch, "E22.21.0.1", {"start": v(561.94, 671.58) * mm, "end": v(727.93, 671.58) * mm});
            skLineSegment(sketch, "E22.21.0.2", {"start": v(561.94, 683.1) * mm, "end": v(561.94, 671.58) * mm});
            skLineSegment(sketch, "E22.21.0.3", {"start": v(727.93, 683.1) * mm, "end": v(727.93, 671.58) * mm});
            skLineSegment(sketch, "E22.direction1", {"start": v(560.62, 1071.63) * mm, "end": v(560.68, 1052.58) * mm, "construction": true});
            skSolve(sketch);
        }
        {
            var Q0;
            Q0 = qSketchRegion(id + "F21", true);
            extrude(context, id + "F22", {"entities" : qUnion([Q0]), "operationType" : NewBodyOperationType.REMOVE, "oppositeDirection" : true, "depth" : 25.4 * mm});
        }
        {
            var Q0;
            Q0=makeQuery(id+"F18.opExtrude","SWEPT_EDGE",EDGE,{"disambiguationData":[OSD([sQuery(id+"F17.wireOp",EDGE,"E15.top"),sQuery(id+"F17.wireOp",EDGE,"E15.right")])]});
            var Q1;
            Q1=makeQuery(id+"F18.opExtrude","SWEPT_EDGE",EDGE,{"disambiguationData":[OSD([sQuery(id+"F17.wireOp",EDGE,"E15.top"),sQuery(id+"F17.wireOp",EDGE,"E15.left")])]});
            var Q2;
            Q2=makeQuery(id+"F18.opExtrude","SWEPT_EDGE",EDGE,{"disambiguationData":[OSD([sQuery(id+"F17.wireOp",EDGE,"E15.bottom"),sQuery(id+"F17.wireOp",EDGE,"E15.right")])]});
            var Q3;
            Q3=makeQuery(id+"F18.opExtrude","SWEPT_EDGE",EDGE,{"disambiguationData":[OSD([sQuery(id+"F17.wireOp",EDGE,"E15.bottom"),sQuery(id+"F17.wireOp",EDGE,"E15.left")])]});
            var Q4;
            Q4=makeQuery(id+"F18.opExtrude","SWEPT_EDGE",EDGE,{"disambiguationData":[OSD([sQuery(id+"F17.wireOp",EDGE,"E14.top"),sQuery(id+"F17.wireOp",EDGE,"E14.right")])]});
            var Q5;
            Q5=makeQuery(id+"F18.opExtrude","SWEPT_EDGE",EDGE,{"disambiguationData":[OSD([sQuery(id+"F17.wireOp",EDGE,"E14.top"),sQuery(id+"F17.wireOp",EDGE,"E14.left")])]});
            var Q6;
            Q6=makeQuery(id+"F18.opExtrude","SWEPT_EDGE",EDGE,{"disambiguationData":[OSD([sQuery(id+"F17.wireOp",EDGE,"E14.bottom"),sQuery(id+"F17.wireOp",EDGE,"E14.right")])]});
            var Q7;
            Q7=makeQuery(id+"F18.opExtrude","SWEPT_EDGE",EDGE,{"disambiguationData":[OSD([sQuery(id+"F17.wireOp",EDGE,"E14.bottom"),sQuery(id+"F17.wireOp",EDGE,"E14.left")])]});
            fillet(context, id + "F23", {"entities" : qUnion([Q0, Q1, Q2, Q3, Q4, Q5, Q6, Q7]), "radius" : 9.52 * mm, "tangentPropagation" : true, "allowEdgeOverflow" : false});
        }
        {
            var Q0;
            Q0=makeQuery(id+"F18.opExtrude","CAP_EDGE",EDGE,{"disambiguationData":[OSD([sQuery(id+"F17.wireOp",EDGE,"E14.bottom")])],"isStart":false});
            var Q1;
            Q1=makeQuery(id+"F18.opExtrude","CAP_EDGE",EDGE,{"disambiguationData":[OSD([sQuery(id+"F17.wireOp",EDGE,"E15.bottom")])],"isStart":false});
            fillet(context, id + "F24", {"entities" : qUnion([Q0, Q1]), "radius" : 5.08 * mm, "tangentPropagation" : true, "allowEdgeOverflow" : false});
        }
    });
